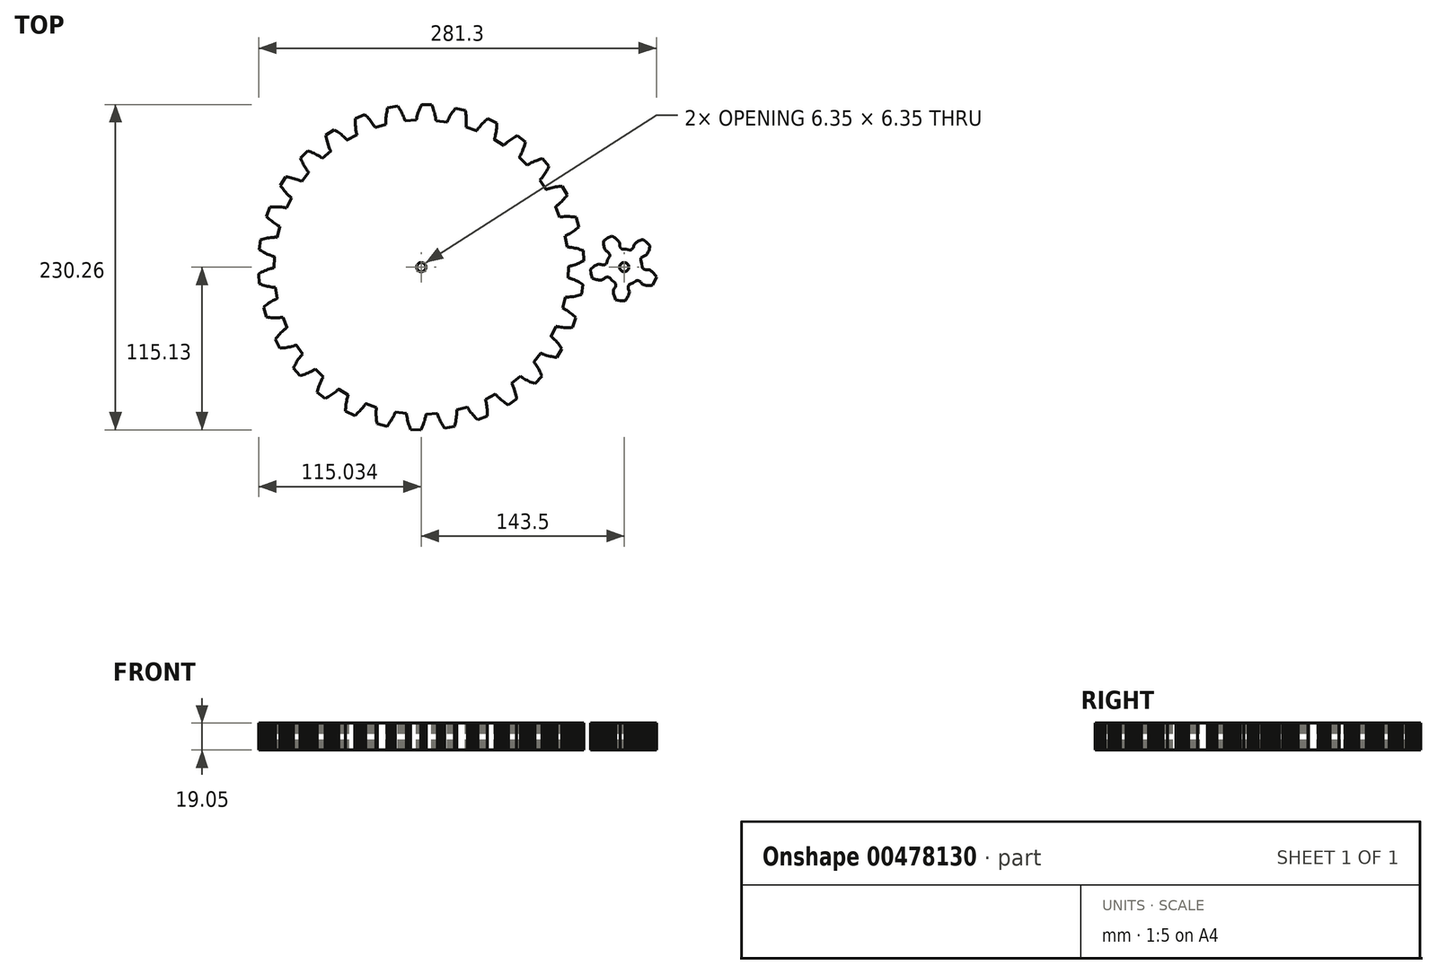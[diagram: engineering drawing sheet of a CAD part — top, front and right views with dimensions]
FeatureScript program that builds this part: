
annotation { "Feature Type Name" : "Feature", "Feature Type Description" : "" }
export const myFeature = defineFeature(function(context is Context, id is Id, definition is map)
    precondition{}
    {
        {
            var Q0;
            Q0=qCreatedBy(makeId("Top.planeOp"),FACE);
            var sketch = newSketch(context, id + "F0", { "sketchPlane" : qUnion([Q0])});
            skLineSegment(sketch, "E0", {"start": v(78.23, -7.5) * mm, "end": v(78.5, -7.55) * mm});
            skLineSegment(sketch, "E1", {"start": v(78.5, -7.55) * mm, "end": v(78.77, -7.62) * mm});
            skLineSegment(sketch, "E2", {"start": v(78.77, -7.62) * mm, "end": v(79.04, -7.7) * mm});
            skLineSegment(sketch, "E3", {"start": v(79.04, -7.7) * mm, "end": v(79.31, -7.77) * mm});
            skLineSegment(sketch, "E4", {"start": v(79.31, -7.77) * mm, "end": v(79.85, -7.93) * mm});
            skLineSegment(sketch, "E5", {"start": v(79.85, -7.93) * mm, "end": v(80.4, -8.1) * mm});
            skLineSegment(sketch, "E6", {"start": v(80.4, -8.1) * mm, "end": v(81.47, -8.5) * mm});
            skLineSegment(sketch, "E7", {"start": v(81.47, -8.5) * mm, "end": v(82.54, -8.93) * mm});
            skLineSegment(sketch, "E8", {"start": v(82.54, -8.93) * mm, "end": v(83.6, -9.4) * mm});
            skLineSegment(sketch, "E9", {"start": v(83.6, -9.4) * mm, "end": v(84.66, -9.91) * mm});
            skLineSegment(sketch, "E10", {"start": v(84.66, -9.91) * mm, "end": v(85.72, -10.46) * mm});
            skLineSegment(sketch, "E11", {"start": v(85.72, -10.46) * mm, "end": v(86.77, -11.05) * mm});
            skLineSegment(sketch, "E12", {"start": v(86.77, -11.05) * mm, "end": v(87.81, -11.66) * mm});
            skLineSegment(sketch, "E13", {"start": v(87.81, -11.66) * mm, "end": v(88.85, -12.31) * mm});
            skLineSegment(sketch, "E14", {"start": v(88.85, -12.31) * mm, "end": v(87.87, -19.4) * mm});
            skLineSegment(sketch, "E15", {"start": v(87.87, -19.4) * mm, "end": v(86.7, -19.74) * mm});
            skLineSegment(sketch, "E16", {"start": v(86.7, -19.74) * mm, "end": v(85.52, -20.05) * mm});
            skLineSegment(sketch, "E17", {"start": v(85.52, -20.05) * mm, "end": v(84.35, -20.32) * mm});
            skLineSegment(sketch, "E18", {"start": v(84.35, -20.32) * mm, "end": v(83.18, -20.56) * mm});
            skLineSegment(sketch, "E19", {"start": v(83.18, -20.56) * mm, "end": v(82.02, -20.77) * mm});
            skLineSegment(sketch, "E20", {"start": v(82.02, -20.77) * mm, "end": v(80.87, -20.93) * mm});
            skLineSegment(sketch, "E21", {"start": v(80.87, -20.93) * mm, "end": v(79.72, -21.06) * mm});
            skLineSegment(sketch, "E22", {"start": v(79.72, -21.06) * mm, "end": v(78.58, -21.14) * mm});
            skLineSegment(sketch, "E23", {"start": v(78.58, -21.14) * mm, "end": v(78.01, -21.16) * mm});
            skLineSegment(sketch, "E24", {"start": v(78.01, -21.16) * mm, "end": v(77.45, -21.17) * mm});
            skLineSegment(sketch, "E25", {"start": v(77.45, -21.17) * mm, "end": v(77.17, -21.17) * mm});
            skLineSegment(sketch, "E26", {"start": v(77.17, -21.17) * mm, "end": v(76.89, -21.16) * mm});
            skLineSegment(sketch, "E27", {"start": v(76.89, -21.16) * mm, "end": v(76.6, -21.15) * mm});
            skLineSegment(sketch, "E28", {"start": v(76.6, -21.15) * mm, "end": v(76.33, -21.14) * mm});
            skLineSegment(sketch, "E29", {"start": v(76.33, -21.14) * mm, "end": v(74.4, -28.92) * mm});
            skLineSegment(sketch, "E30", {"start": v(74.4, -28.92) * mm, "end": v(74.65, -29.03) * mm});
            skLineSegment(sketch, "E31", {"start": v(74.65, -29.03) * mm, "end": v(74.9, -29.16) * mm});
            skLineSegment(sketch, "E32", {"start": v(74.9, -29.16) * mm, "end": v(75.16, -29.28) * mm});
            skLineSegment(sketch, "E33", {"start": v(75.16, -29.28) * mm, "end": v(75.4, -29.41) * mm});
            skLineSegment(sketch, "E34", {"start": v(75.4, -29.41) * mm, "end": v(75.9, -29.68) * mm});
            skLineSegment(sketch, "E35", {"start": v(75.9, -29.68) * mm, "end": v(76.39, -29.97) * mm});
            skLineSegment(sketch, "E36", {"start": v(76.39, -29.97) * mm, "end": v(77.36, -30.57) * mm});
            skLineSegment(sketch, "E37", {"start": v(77.36, -30.57) * mm, "end": v(78.32, -31.22) * mm});
            skLineSegment(sketch, "E38", {"start": v(78.32, -31.22) * mm, "end": v(79.26, -31.9) * mm});
            skLineSegment(sketch, "E39", {"start": v(79.26, -31.9) * mm, "end": v(80.2, -32.63) * mm});
            skLineSegment(sketch, "E40", {"start": v(80.2, -32.63) * mm, "end": v(81.11, -33.38) * mm});
            skLineSegment(sketch, "E41", {"start": v(81.11, -33.38) * mm, "end": v(82.02, -34.17) * mm});
            skLineSegment(sketch, "E42", {"start": v(82.02, -34.17) * mm, "end": v(82.91, -35) * mm});
            skLineSegment(sketch, "E43", {"start": v(82.91, -35) * mm, "end": v(83.8, -35.84) * mm});
            skLineSegment(sketch, "E44", {"start": v(83.8, -35.84) * mm, "end": v(81.35, -42.57) * mm});
            skLineSegment(sketch, "E45", {"start": v(81.35, -42.57) * mm, "end": v(80.13, -42.66) * mm});
            skLineSegment(sketch, "E46", {"start": v(80.13, -42.66) * mm, "end": v(78.92, -42.72) * mm});
            skLineSegment(sketch, "E47", {"start": v(78.92, -42.72) * mm, "end": v(77.72, -42.74) * mm});
            skLineSegment(sketch, "E48", {"start": v(77.72, -42.74) * mm, "end": v(76.53, -42.73) * mm});
            skLineSegment(sketch, "E49", {"start": v(76.53, -42.73) * mm, "end": v(75.35, -42.7) * mm});
            skLineSegment(sketch, "E50", {"start": v(75.35, -42.7) * mm, "end": v(74.19, -42.61) * mm});
            skLineSegment(sketch, "E51", {"start": v(74.19, -42.61) * mm, "end": v(73.04, -42.5) * mm});
            skLineSegment(sketch, "E52", {"start": v(73.04, -42.5) * mm, "end": v(71.9, -42.34) * mm});
            skLineSegment(sketch, "E53", {"start": v(71.9, -42.34) * mm, "end": v(71.35, -42.24) * mm});
            skLineSegment(sketch, "E54", {"start": v(71.35, -42.24) * mm, "end": v(70.8, -42.13) * mm});
            skLineSegment(sketch, "E55", {"start": v(70.8, -42.13) * mm, "end": v(70.52, -42.07) * mm});
            skLineSegment(sketch, "E56", {"start": v(70.52, -42.07) * mm, "end": v(70.25, -42.01) * mm});
            skLineSegment(sketch, "E57", {"start": v(70.25, -42.01) * mm, "end": v(69.98, -41.94) * mm});
            skLineSegment(sketch, "E58", {"start": v(69.98, -41.94) * mm, "end": v(69.7, -41.87) * mm});
            skLineSegment(sketch, "E59", {"start": v(69.7, -41.87) * mm, "end": v(66.2, -49.08) * mm});
            skLineSegment(sketch, "E60", {"start": v(66.2, -49.08) * mm, "end": v(66.43, -49.25) * mm});
            skLineSegment(sketch, "E61", {"start": v(66.43, -49.25) * mm, "end": v(66.65, -49.42) * mm});
            skLineSegment(sketch, "E62", {"start": v(66.65, -49.42) * mm, "end": v(66.87, -49.6) * mm});
            skLineSegment(sketch, "E63", {"start": v(66.87, -49.6) * mm, "end": v(67.08, -49.77) * mm});
            skLineSegment(sketch, "E64", {"start": v(67.08, -49.77) * mm, "end": v(67.5, -50.14) * mm});
            skLineSegment(sketch, "E65", {"start": v(67.5, -50.14) * mm, "end": v(67.93, -50.52) * mm});
            skLineSegment(sketch, "E66", {"start": v(67.93, -50.52) * mm, "end": v(68.75, -51.31) * mm});
            skLineSegment(sketch, "E67", {"start": v(68.75, -51.31) * mm, "end": v(69.56, -52.15) * mm});
            skLineSegment(sketch, "E68", {"start": v(69.56, -52.15) * mm, "end": v(70.34, -53.01) * mm});
            skLineSegment(sketch, "E69", {"start": v(70.34, -53.01) * mm, "end": v(71.1, -53.91) * mm});
            skLineSegment(sketch, "E70", {"start": v(71.1, -53.91) * mm, "end": v(71.84, -54.84) * mm});
            skLineSegment(sketch, "E71", {"start": v(71.84, -54.84) * mm, "end": v(72.56, -55.8) * mm});
            skLineSegment(sketch, "E72", {"start": v(72.56, -55.8) * mm, "end": v(73.26, -56.8) * mm});
            skLineSegment(sketch, "E73", {"start": v(73.26, -56.8) * mm, "end": v(73.95, -57.8) * mm});
            skLineSegment(sketch, "E74", {"start": v(73.95, -57.8) * mm, "end": v(70.17, -63.88) * mm});
            skLineSegment(sketch, "E75", {"start": v(70.17, -63.88) * mm, "end": v(68.95, -63.71) * mm});
            skLineSegment(sketch, "E76", {"start": v(68.95, -63.71) * mm, "end": v(67.75, -63.52) * mm});
            skLineSegment(sketch, "E77", {"start": v(67.75, -63.52) * mm, "end": v(66.57, -63.3) * mm});
            skLineSegment(sketch, "E78", {"start": v(66.57, -63.3) * mm, "end": v(65.41, -63.04) * mm});
            skLineSegment(sketch, "E79", {"start": v(65.41, -63.04) * mm, "end": v(64.27, -62.75) * mm});
            skLineSegment(sketch, "E80", {"start": v(64.27, -62.75) * mm, "end": v(63.15, -62.43) * mm});
            skLineSegment(sketch, "E81", {"start": v(63.15, -62.43) * mm, "end": v(62.05, -62.08) * mm});
            skLineSegment(sketch, "E82", {"start": v(62.05, -62.08) * mm, "end": v(60.97, -61.69) * mm});
            skLineSegment(sketch, "E83", {"start": v(60.97, -61.69) * mm, "end": v(60.45, -61.48) * mm});
            skLineSegment(sketch, "E84", {"start": v(60.45, -61.48) * mm, "end": v(59.93, -61.26) * mm});
            skLineSegment(sketch, "E85", {"start": v(59.93, -61.26) * mm, "end": v(59.67, -61.14) * mm});
            skLineSegment(sketch, "E86", {"start": v(59.67, -61.14) * mm, "end": v(59.42, -61.02) * mm});
            skLineSegment(sketch, "E87", {"start": v(59.42, -61.02) * mm, "end": v(59.17, -60.9) * mm});
            skLineSegment(sketch, "E88", {"start": v(59.17, -60.9) * mm, "end": v(58.92, -60.78) * mm});
            skLineSegment(sketch, "E89", {"start": v(58.92, -60.78) * mm, "end": v(54, -67.1) * mm});
            skLineSegment(sketch, "E90", {"start": v(54, -67.1) * mm, "end": v(54.18, -67.3) * mm});
            skLineSegment(sketch, "E91", {"start": v(54.18, -67.3) * mm, "end": v(54.36, -67.52) * mm});
            skLineSegment(sketch, "E92", {"start": v(54.36, -67.52) * mm, "end": v(54.53, -67.74) * mm});
            skLineSegment(sketch, "E93", {"start": v(54.53, -67.74) * mm, "end": v(54.7, -67.96) * mm});
            skLineSegment(sketch, "E94", {"start": v(54.7, -67.96) * mm, "end": v(55.05, -68.4) * mm});
            skLineSegment(sketch, "E95", {"start": v(55.05, -68.4) * mm, "end": v(55.38, -68.87) * mm});
            skLineSegment(sketch, "E96", {"start": v(55.38, -68.87) * mm, "end": v(56.02, -69.81) * mm});
            skLineSegment(sketch, "E97", {"start": v(56.02, -69.81) * mm, "end": v(56.63, -70.8) * mm});
            skLineSegment(sketch, "E98", {"start": v(56.63, -70.8) * mm, "end": v(57.22, -71.8) * mm});
            skLineSegment(sketch, "E99", {"start": v(57.22, -71.8) * mm, "end": v(57.77, -72.84) * mm});
            skLineSegment(sketch, "E100", {"start": v(57.77, -72.84) * mm, "end": v(58.3, -73.9) * mm});
            skLineSegment(sketch, "E101", {"start": v(58.3, -73.9) * mm, "end": v(58.81, -75) * mm});
            skLineSegment(sketch, "E102", {"start": v(58.81, -75) * mm, "end": v(59.3, -76.1) * mm});
            skLineSegment(sketch, "E103", {"start": v(59.3, -76.1) * mm, "end": v(59.76, -77.24) * mm});
            skLineSegment(sketch, "E104", {"start": v(59.76, -77.24) * mm, "end": v(54.8, -82.4) * mm});
            skLineSegment(sketch, "E105", {"start": v(54.8, -82.4) * mm, "end": v(53.64, -81.98) * mm});
            skLineSegment(sketch, "E106", {"start": v(53.64, -81.98) * mm, "end": v(52.5, -81.54) * mm});
            skLineSegment(sketch, "E107", {"start": v(52.5, -81.54) * mm, "end": v(51.4, -81.08) * mm});
            skLineSegment(sketch, "E108", {"start": v(51.4, -81.08) * mm, "end": v(50.32, -80.59) * mm});
            skLineSegment(sketch, "E109", {"start": v(50.32, -80.59) * mm, "end": v(49.26, -80.07) * mm});
            skLineSegment(sketch, "E110", {"start": v(49.26, -80.07) * mm, "end": v(48.23, -79.52) * mm});
            skLineSegment(sketch, "E111", {"start": v(48.23, -79.52) * mm, "end": v(47.22, -78.95) * mm});
            skLineSegment(sketch, "E112", {"start": v(47.22, -78.95) * mm, "end": v(46.25, -78.34) * mm});
            skLineSegment(sketch, "E113", {"start": v(46.25, -78.34) * mm, "end": v(45.78, -78.03) * mm});
            skLineSegment(sketch, "E114", {"start": v(45.78, -78.03) * mm, "end": v(45.32, -77.7) * mm});
            skLineSegment(sketch, "E115", {"start": v(45.32, -77.7) * mm, "end": v(45.1, -77.54) * mm});
            skLineSegment(sketch, "E116", {"start": v(45.1, -77.54) * mm, "end": v(44.87, -77.37) * mm});
            skLineSegment(sketch, "E117", {"start": v(44.87, -77.37) * mm, "end": v(44.65, -77.2) * mm});
            skLineSegment(sketch, "E118", {"start": v(44.65, -77.2) * mm, "end": v(44.43, -77.02) * mm});
            skLineSegment(sketch, "E119", {"start": v(44.43, -77.02) * mm, "end": v(38.3, -82.18) * mm});
            skLineSegment(sketch, "E120", {"start": v(38.3, -82.18) * mm, "end": v(38.44, -82.43) * mm});
            skLineSegment(sketch, "E121", {"start": v(38.44, -82.43) * mm, "end": v(38.57, -82.67) * mm});
            skLineSegment(sketch, "E122", {"start": v(38.57, -82.67) * mm, "end": v(38.7, -82.92) * mm});
            skLineSegment(sketch, "E123", {"start": v(38.7, -82.92) * mm, "end": v(38.82, -83.17) * mm});
            skLineSegment(sketch, "E124", {"start": v(38.82, -83.17) * mm, "end": v(39.06, -83.68) * mm});
            skLineSegment(sketch, "E125", {"start": v(39.06, -83.68) * mm, "end": v(39.3, -84.2) * mm});
            skLineSegment(sketch, "E126", {"start": v(39.3, -84.2) * mm, "end": v(39.72, -85.26) * mm});
            skLineSegment(sketch, "E127", {"start": v(39.72, -85.26) * mm, "end": v(40.12, -86.35) * mm});
            skLineSegment(sketch, "E128", {"start": v(40.12, -86.35) * mm, "end": v(40.48, -87.46) * mm});
            skLineSegment(sketch, "E129", {"start": v(40.48, -87.46) * mm, "end": v(40.8, -88.59) * mm});
            skLineSegment(sketch, "E130", {"start": v(40.8, -88.59) * mm, "end": v(41.1, -89.74) * mm});
            skLineSegment(sketch, "E131", {"start": v(41.1, -89.74) * mm, "end": v(41.37, -90.91) * mm});
            skLineSegment(sketch, "E132", {"start": v(41.37, -90.91) * mm, "end": v(41.62, -92.1) * mm});
            skLineSegment(sketch, "E133", {"start": v(41.62, -92.1) * mm, "end": v(41.83, -93.3) * mm});
            skLineSegment(sketch, "E134", {"start": v(41.83, -93.3) * mm, "end": v(35.9, -97.32) * mm});
            skLineSegment(sketch, "E135", {"start": v(35.9, -97.32) * mm, "end": v(34.86, -96.67) * mm});
            skLineSegment(sketch, "E136", {"start": v(34.86, -96.67) * mm, "end": v(33.85, -96) * mm});
            skLineSegment(sketch, "E137", {"start": v(33.85, -96) * mm, "end": v(32.86, -95.32) * mm});
            skLineSegment(sketch, "E138", {"start": v(32.86, -95.32) * mm, "end": v(31.9, -94.61) * mm});
            skLineSegment(sketch, "E139", {"start": v(31.9, -94.61) * mm, "end": v(30.97, -93.89) * mm});
            skLineSegment(sketch, "E140", {"start": v(30.97, -93.89) * mm, "end": v(30.08, -93.14) * mm});
            skLineSegment(sketch, "E141", {"start": v(30.08, -93.14) * mm, "end": v(29.22, -92.37) * mm});
            skLineSegment(sketch, "E142", {"start": v(29.22, -92.37) * mm, "end": v(28.4, -91.58) * mm});
            skLineSegment(sketch, "E143", {"start": v(28.4, -91.58) * mm, "end": v(28, -91.17) * mm});
            skLineSegment(sketch, "E144", {"start": v(28, -91.17) * mm, "end": v(27.62, -90.76) * mm});
            skLineSegment(sketch, "E145", {"start": v(27.62, -90.76) * mm, "end": v(27.43, -90.55) * mm});
            skLineSegment(sketch, "E146", {"start": v(27.43, -90.55) * mm, "end": v(27.25, -90.33) * mm});
            skLineSegment(sketch, "E147", {"start": v(27.25, -90.33) * mm, "end": v(27.07, -90.12) * mm});
            skLineSegment(sketch, "E148", {"start": v(27.07, -90.12) * mm, "end": v(26.89, -89.9) * mm});
            skLineSegment(sketch, "E149", {"start": v(26.89, -89.9) * mm, "end": v(19.82, -93.68) * mm});
            skLineSegment(sketch, "E150", {"start": v(19.82, -93.68) * mm, "end": v(19.9, -93.94) * mm});
            skLineSegment(sketch, "E151", {"start": v(19.9, -93.94) * mm, "end": v(19.98, -94.21) * mm});
            skLineSegment(sketch, "E152", {"start": v(19.98, -94.21) * mm, "end": v(20.05, -94.48) * mm});
            skLineSegment(sketch, "E153", {"start": v(20.05, -94.48) * mm, "end": v(20.12, -94.75) * mm});
            skLineSegment(sketch, "E154", {"start": v(20.12, -94.75) * mm, "end": v(20.25, -95.3) * mm});
            skLineSegment(sketch, "E155", {"start": v(20.25, -95.3) * mm, "end": v(20.37, -95.86) * mm});
            skLineSegment(sketch, "E156", {"start": v(20.37, -95.86) * mm, "end": v(20.57, -96.98) * mm});
            skLineSegment(sketch, "E157", {"start": v(20.57, -96.98) * mm, "end": v(20.73, -98.13) * mm});
            skLineSegment(sketch, "E158", {"start": v(20.73, -98.13) * mm, "end": v(20.85, -99.29) * mm});
            skLineSegment(sketch, "E159", {"start": v(20.85, -99.29) * mm, "end": v(20.94, -100.46) * mm});
            skLineSegment(sketch, "E160", {"start": v(20.94, -100.46) * mm, "end": v(20.99, -101.65) * mm});
            skLineSegment(sketch, "E161", {"start": v(20.99, -101.65) * mm, "end": v(21, -102.85) * mm});
            skLineSegment(sketch, "E162", {"start": v(21, -102.85) * mm, "end": v(21, -104.06) * mm});
            skLineSegment(sketch, "E163", {"start": v(21, -104.06) * mm, "end": v(20.96, -105.29) * mm});
            skLineSegment(sketch, "E164", {"start": v(20.96, -105.29) * mm, "end": v(14.32, -107.98) * mm});
            skLineSegment(sketch, "E165", {"start": v(14.32, -107.98) * mm, "end": v(13.44, -107.13) * mm});
            skLineSegment(sketch, "E166", {"start": v(13.44, -107.13) * mm, "end": v(12.59, -106.27) * mm});
            skLineSegment(sketch, "E167", {"start": v(12.59, -106.27) * mm, "end": v(11.77, -105.4) * mm});
            skLineSegment(sketch, "E168", {"start": v(11.77, -105.4) * mm, "end": v(10.97, -104.5) * mm});
            skLineSegment(sketch, "E169", {"start": v(10.97, -104.5) * mm, "end": v(10.22, -103.6) * mm});
            skLineSegment(sketch, "E170", {"start": v(10.22, -103.6) * mm, "end": v(9.5, -102.68) * mm});
            skLineSegment(sketch, "E171", {"start": v(9.5, -102.68) * mm, "end": v(8.82, -101.75) * mm});
            skLineSegment(sketch, "E172", {"start": v(8.82, -101.75) * mm, "end": v(8.18, -100.8) * mm});
            skLineSegment(sketch, "E173", {"start": v(8.18, -100.8) * mm, "end": v(7.87, -100.32) * mm});
            skLineSegment(sketch, "E174", {"start": v(7.87, -100.32) * mm, "end": v(7.58, -99.84) * mm});
            skLineSegment(sketch, "E175", {"start": v(7.58, -99.84) * mm, "end": v(7.44, -99.6) * mm});
            skLineSegment(sketch, "E176", {"start": v(7.44, -99.6) * mm, "end": v(7.3, -99.35) * mm});
            skLineSegment(sketch, "E177", {"start": v(7.3, -99.35) * mm, "end": v(7.18, -99.1) * mm});
            skLineSegment(sketch, "E178", {"start": v(7.18, -99.1) * mm, "end": v(7.05, -98.86) * mm});
            skLineSegment(sketch, "E179", {"start": v(7.05, -98.86) * mm, "end": v(-0.65, -101.08) * mm});
            skLineSegment(sketch, "E180", {"start": v(-0.65, -101.08) * mm, "end": v(-0.63, -101.35) * mm});
            skLineSegment(sketch, "E181", {"start": v(-0.63, -101.35) * mm, "end": v(-0.6, -101.63) * mm});
            skLineSegment(sketch, "E182", {"start": v(-0.6, -101.63) * mm, "end": v(-0.6, -101.91) * mm});
            skLineSegment(sketch, "E183", {"start": v(-0.6, -101.91) * mm, "end": v(-0.58, -102.2) * mm});
            skLineSegment(sketch, "E184", {"start": v(-0.58, -102.2) * mm, "end": v(-0.57, -102.76) * mm});
            skLineSegment(sketch, "E185", {"start": v(-0.57, -102.76) * mm, "end": v(-0.57, -103.32) * mm});
            skLineSegment(sketch, "E186", {"start": v(-0.57, -103.32) * mm, "end": v(-0.6, -104.47) * mm});
            skLineSegment(sketch, "E187", {"start": v(-0.6, -104.47) * mm, "end": v(-0.69, -105.62) * mm});
            skLineSegment(sketch, "E188", {"start": v(-0.69, -105.62) * mm, "end": v(-0.8, -106.78) * mm});
            skLineSegment(sketch, "E189", {"start": v(-0.8, -106.78) * mm, "end": v(-0.97, -107.94) * mm});
            skLineSegment(sketch, "E190", {"start": v(-0.97, -107.94) * mm, "end": v(-1.16, -109.12) * mm});
            skLineSegment(sketch, "E191", {"start": v(-1.16, -109.12) * mm, "end": v(-1.4, -110.3) * mm});
            skLineSegment(sketch, "E192", {"start": v(-1.4, -110.3) * mm, "end": v(-1.66, -111.48) * mm});
            skLineSegment(sketch, "E193", {"start": v(-1.66, -111.48) * mm, "end": v(-1.95, -112.67) * mm});
            skLineSegment(sketch, "E194", {"start": v(-1.95, -112.67) * mm, "end": v(-9, -113.92) * mm});
            skLineSegment(sketch, "E195", {"start": v(-9, -113.92) * mm, "end": v(-9.69, -112.9) * mm});
            skLineSegment(sketch, "E196", {"start": v(-9.69, -112.9) * mm, "end": v(-10.34, -111.89) * mm});
            skLineSegment(sketch, "E197", {"start": v(-10.34, -111.89) * mm, "end": v(-10.96, -110.86) * mm});
            skLineSegment(sketch, "E198", {"start": v(-10.96, -110.86) * mm, "end": v(-11.55, -109.83) * mm});
            skLineSegment(sketch, "E199", {"start": v(-11.55, -109.83) * mm, "end": v(-12.1, -108.79) * mm});
            skLineSegment(sketch, "E200", {"start": v(-12.1, -108.79) * mm, "end": v(-12.62, -107.74) * mm});
            skLineSegment(sketch, "E201", {"start": v(-12.62, -107.74) * mm, "end": v(-13.1, -106.69) * mm});
            skLineSegment(sketch, "E202", {"start": v(-13.1, -106.69) * mm, "end": v(-13.52, -105.63) * mm});
            skLineSegment(sketch, "E203", {"start": v(-13.52, -105.63) * mm, "end": v(-13.72, -105.1) * mm});
            skLineSegment(sketch, "E204", {"start": v(-13.72, -105.1) * mm, "end": v(-13.9, -104.56) * mm});
            skLineSegment(sketch, "E205", {"start": v(-13.9, -104.56) * mm, "end": v(-13.99, -104.3) * mm});
            skLineSegment(sketch, "E206", {"start": v(-13.99, -104.3) * mm, "end": v(-14.07, -104.03) * mm});
            skLineSegment(sketch, "E207", {"start": v(-14.07, -104.03) * mm, "end": v(-14.14, -103.76) * mm});
            skLineSegment(sketch, "E208", {"start": v(-14.14, -103.76) * mm, "end": v(-14.22, -103.49) * mm});
            skLineSegment(sketch, "E209", {"start": v(-14.22, -103.49) * mm, "end": v(-22.21, -104.06) * mm});
            skLineSegment(sketch, "E210", {"start": v(-22.21, -104.06) * mm, "end": v(-22.24, -104.33) * mm});
            skLineSegment(sketch, "E211", {"start": v(-22.24, -104.33) * mm, "end": v(-22.28, -104.61) * mm});
            skLineSegment(sketch, "E212", {"start": v(-22.28, -104.61) * mm, "end": v(-22.33, -104.89) * mm});
            skLineSegment(sketch, "E213", {"start": v(-22.33, -104.89) * mm, "end": v(-22.37, -105.17) * mm});
            skLineSegment(sketch, "E214", {"start": v(-22.37, -105.17) * mm, "end": v(-22.48, -105.72) * mm});
            skLineSegment(sketch, "E215", {"start": v(-22.48, -105.72) * mm, "end": v(-22.6, -106.27) * mm});
            skLineSegment(sketch, "E216", {"start": v(-22.6, -106.27) * mm, "end": v(-22.87, -107.38) * mm});
            skLineSegment(sketch, "E217", {"start": v(-22.87, -107.38) * mm, "end": v(-23.19, -108.5) * mm});
            skLineSegment(sketch, "E218", {"start": v(-23.19, -108.5) * mm, "end": v(-23.55, -109.6) * mm});
            skLineSegment(sketch, "E219", {"start": v(-23.55, -109.6) * mm, "end": v(-23.95, -110.71) * mm});
            skLineSegment(sketch, "E220", {"start": v(-23.95, -110.71) * mm, "end": v(-24.38, -111.82) * mm});
            skLineSegment(sketch, "E221", {"start": v(-24.38, -111.82) * mm, "end": v(-24.85, -112.92) * mm});
            skLineSegment(sketch, "E222", {"start": v(-24.85, -112.92) * mm, "end": v(-25.36, -114.03) * mm});
            skLineSegment(sketch, "E223", {"start": v(-25.36, -114.03) * mm, "end": v(-25.9, -115.13) * mm});
            skLineSegment(sketch, "E224", {"start": v(-25.9, -115.13) * mm, "end": v(-33.05, -114.89) * mm});
            skLineSegment(sketch, "E225", {"start": v(-33.05, -114.89) * mm, "end": v(-33.5, -113.75) * mm});
            skLineSegment(sketch, "E226", {"start": v(-33.5, -113.75) * mm, "end": v(-33.94, -112.62) * mm});
            skLineSegment(sketch, "E227", {"start": v(-33.94, -112.62) * mm, "end": v(-34.33, -111.48) * mm});
            skLineSegment(sketch, "E228", {"start": v(-34.33, -111.48) * mm, "end": v(-34.7, -110.35) * mm});
            skLineSegment(sketch, "E229", {"start": v(-34.7, -110.35) * mm, "end": v(-35.02, -109.22) * mm});
            skLineSegment(sketch, "E230", {"start": v(-35.02, -109.22) * mm, "end": v(-35.3, -108.09) * mm});
            skLineSegment(sketch, "E231", {"start": v(-35.3, -108.09) * mm, "end": v(-35.55, -106.96) * mm});
            skLineSegment(sketch, "E232", {"start": v(-35.55, -106.96) * mm, "end": v(-35.75, -105.83) * mm});
            skLineSegment(sketch, "E233", {"start": v(-35.75, -105.83) * mm, "end": v(-35.83, -105.27) * mm});
            skLineSegment(sketch, "E234", {"start": v(-35.83, -105.27) * mm, "end": v(-35.9, -104.71) * mm});
            skLineSegment(sketch, "E235", {"start": v(-35.9, -104.71) * mm, "end": v(-35.92, -104.43) * mm});
            skLineSegment(sketch, "E236", {"start": v(-35.92, -104.43) * mm, "end": v(-35.95, -104.15) * mm});
            skLineSegment(sketch, "E237", {"start": v(-35.95, -104.15) * mm, "end": v(-35.97, -103.87) * mm});
            skLineSegment(sketch, "E238", {"start": v(-35.97, -103.87) * mm, "end": v(-35.98, -103.6) * mm});
            skLineSegment(sketch, "E239", {"start": v(-35.98, -103.6) * mm, "end": v(-43.92, -102.5) * mm});
            skLineSegment(sketch, "E240", {"start": v(-43.92, -102.5) * mm, "end": v(-44.01, -102.76) * mm});
            skLineSegment(sketch, "E241", {"start": v(-44.01, -102.76) * mm, "end": v(-44.1, -103.02) * mm});
            skLineSegment(sketch, "E242", {"start": v(-44.1, -103.02) * mm, "end": v(-44.2, -103.28) * mm});
            skLineSegment(sketch, "E243", {"start": v(-44.2, -103.28) * mm, "end": v(-44.3, -103.54) * mm});
            skLineSegment(sketch, "E244", {"start": v(-44.3, -103.54) * mm, "end": v(-44.53, -104.06) * mm});
            skLineSegment(sketch, "E245", {"start": v(-44.53, -104.06) * mm, "end": v(-44.76, -104.58) * mm});
            skLineSegment(sketch, "E246", {"start": v(-44.76, -104.58) * mm, "end": v(-45.26, -105.6) * mm});
            skLineSegment(sketch, "E247", {"start": v(-45.26, -105.6) * mm, "end": v(-45.8, -106.63) * mm});
            skLineSegment(sketch, "E248", {"start": v(-45.8, -106.63) * mm, "end": v(-46.38, -107.64) * mm});
            skLineSegment(sketch, "E249", {"start": v(-46.38, -107.64) * mm, "end": v(-47, -108.64) * mm});
            skLineSegment(sketch, "E250", {"start": v(-47, -108.64) * mm, "end": v(-47.66, -109.63) * mm});
            skLineSegment(sketch, "E251", {"start": v(-47.66, -109.63) * mm, "end": v(-48.35, -110.61) * mm});
            skLineSegment(sketch, "E252", {"start": v(-48.35, -110.61) * mm, "end": v(-49.07, -111.59) * mm});
            skLineSegment(sketch, "E253", {"start": v(-49.07, -111.59) * mm, "end": v(-49.83, -112.56) * mm});
            skLineSegment(sketch, "E254", {"start": v(-49.83, -112.56) * mm, "end": v(-56.77, -110.83) * mm});
            skLineSegment(sketch, "E255", {"start": v(-56.77, -110.83) * mm, "end": v(-56.99, -109.63) * mm});
            skLineSegment(sketch, "E256", {"start": v(-56.99, -109.63) * mm, "end": v(-57.17, -108.43) * mm});
            skLineSegment(sketch, "E257", {"start": v(-57.17, -108.43) * mm, "end": v(-57.32, -107.24) * mm});
            skLineSegment(sketch, "E258", {"start": v(-57.32, -107.24) * mm, "end": v(-57.44, -106.05) * mm});
            skLineSegment(sketch, "E259", {"start": v(-57.44, -106.05) * mm, "end": v(-57.52, -104.88) * mm});
            skLineSegment(sketch, "E260", {"start": v(-57.52, -104.88) * mm, "end": v(-57.56, -103.71) * mm});
            skLineSegment(sketch, "E261", {"start": v(-57.56, -103.71) * mm, "end": v(-57.57, -102.56) * mm});
            skLineSegment(sketch, "E262", {"start": v(-57.57, -102.56) * mm, "end": v(-57.53, -101.41) * mm});
            skLineSegment(sketch, "E263", {"start": v(-57.53, -101.41) * mm, "end": v(-57.5, -100.85) * mm});
            skLineSegment(sketch, "E264", {"start": v(-57.5, -100.85) * mm, "end": v(-57.44, -100.29) * mm});
            skLineSegment(sketch, "E265", {"start": v(-57.44, -100.29) * mm, "end": v(-57.41, -100) * mm});
            skLineSegment(sketch, "E266", {"start": v(-57.41, -100) * mm, "end": v(-57.38, -99.73) * mm});
            skLineSegment(sketch, "E267", {"start": v(-57.38, -99.73) * mm, "end": v(-57.34, -99.45) * mm});
            skLineSegment(sketch, "E268", {"start": v(-57.34, -99.45) * mm, "end": v(-57.3, -99.18) * mm});
            skLineSegment(sketch, "E269", {"start": v(-57.3, -99.18) * mm, "end": v(-64.83, -96.45) * mm});
            skLineSegment(sketch, "E270", {"start": v(-64.83, -96.45) * mm, "end": v(-64.97, -96.69) * mm});
            skLineSegment(sketch, "E271", {"start": v(-64.97, -96.69) * mm, "end": v(-65.12, -96.92) * mm});
            skLineSegment(sketch, "E272", {"start": v(-65.12, -96.92) * mm, "end": v(-65.27, -97.16) * mm});
            skLineSegment(sketch, "E273", {"start": v(-65.27, -97.16) * mm, "end": v(-65.43, -97.4) * mm});
            skLineSegment(sketch, "E274", {"start": v(-65.43, -97.4) * mm, "end": v(-65.75, -97.86) * mm});
            skLineSegment(sketch, "E275", {"start": v(-65.75, -97.86) * mm, "end": v(-66.08, -98.31) * mm});
            skLineSegment(sketch, "E276", {"start": v(-66.08, -98.31) * mm, "end": v(-66.78, -99.22) * mm});
            skLineSegment(sketch, "E277", {"start": v(-66.78, -99.22) * mm, "end": v(-67.53, -100.1) * mm});
            skLineSegment(sketch, "E278", {"start": v(-67.53, -100.1) * mm, "end": v(-68.3, -100.97) * mm});
            skLineSegment(sketch, "E279", {"start": v(-68.3, -100.97) * mm, "end": v(-69.12, -101.82) * mm});
            skLineSegment(sketch, "E280", {"start": v(-69.12, -101.82) * mm, "end": v(-69.97, -102.65) * mm});
            skLineSegment(sketch, "E281", {"start": v(-69.97, -102.65) * mm, "end": v(-70.85, -103.47) * mm});
            skLineSegment(sketch, "E282", {"start": v(-70.85, -103.47) * mm, "end": v(-71.76, -104.27) * mm});
            skLineSegment(sketch, "E283", {"start": v(-71.76, -104.27) * mm, "end": v(-72.7, -105.06) * mm});
            skLineSegment(sketch, "E284", {"start": v(-72.7, -105.06) * mm, "end": v(-79.13, -101.93) * mm});
            skLineSegment(sketch, "E285", {"start": v(-79.13, -101.93) * mm, "end": v(-79.1, -100.7) * mm});
            skLineSegment(sketch, "E286", {"start": v(-79.1, -100.7) * mm, "end": v(-79.03, -99.5) * mm});
            skLineSegment(sketch, "E287", {"start": v(-79.03, -99.5) * mm, "end": v(-78.92, -98.3) * mm});
            skLineSegment(sketch, "E288", {"start": v(-78.92, -98.3) * mm, "end": v(-78.8, -97.12) * mm});
            skLineSegment(sketch, "E289", {"start": v(-78.8, -97.12) * mm, "end": v(-78.63, -95.95) * mm});
            skLineSegment(sketch, "E290", {"start": v(-78.63, -95.95) * mm, "end": v(-78.43, -94.8) * mm});
            skLineSegment(sketch, "E291", {"start": v(-78.43, -94.8) * mm, "end": v(-78.2, -93.67) * mm});
            skLineSegment(sketch, "E292", {"start": v(-78.2, -93.67) * mm, "end": v(-77.92, -92.56) * mm});
            skLineSegment(sketch, "E293", {"start": v(-77.92, -92.56) * mm, "end": v(-77.76, -92.02) * mm});
            skLineSegment(sketch, "E294", {"start": v(-77.76, -92.02) * mm, "end": v(-77.6, -91.48) * mm});
            skLineSegment(sketch, "E295", {"start": v(-77.6, -91.48) * mm, "end": v(-77.5, -91.21) * mm});
            skLineSegment(sketch, "E296", {"start": v(-77.5, -91.21) * mm, "end": v(-77.42, -90.95) * mm});
            skLineSegment(sketch, "E297", {"start": v(-77.42, -90.95) * mm, "end": v(-77.32, -90.68) * mm});
            skLineSegment(sketch, "E298", {"start": v(-77.32, -90.68) * mm, "end": v(-77.22, -90.42) * mm});
            skLineSegment(sketch, "E299", {"start": v(-77.22, -90.42) * mm, "end": v(-84.02, -86.19) * mm});
            skLineSegment(sketch, "E300", {"start": v(-84.02, -86.19) * mm, "end": v(-84.21, -86.4) * mm});
            skLineSegment(sketch, "E301", {"start": v(-84.21, -86.4) * mm, "end": v(-84.4, -86.6) * mm});
            skLineSegment(sketch, "E302", {"start": v(-84.4, -86.6) * mm, "end": v(-84.6, -86.8) * mm});
            skLineSegment(sketch, "E303", {"start": v(-84.6, -86.8) * mm, "end": v(-84.8, -86.99) * mm});
            skLineSegment(sketch, "E304", {"start": v(-84.8, -86.99) * mm, "end": v(-85.22, -87.37) * mm});
            skLineSegment(sketch, "E305", {"start": v(-85.22, -87.37) * mm, "end": v(-85.64, -87.75) * mm});
            skLineSegment(sketch, "E306", {"start": v(-85.64, -87.75) * mm, "end": v(-86.51, -88.49) * mm});
            skLineSegment(sketch, "E307", {"start": v(-86.51, -88.49) * mm, "end": v(-87.42, -89.2) * mm});
            skLineSegment(sketch, "E308", {"start": v(-87.42, -89.2) * mm, "end": v(-88.37, -89.88) * mm});
            skLineSegment(sketch, "E309", {"start": v(-88.37, -89.88) * mm, "end": v(-89.34, -90.55) * mm});
            skLineSegment(sketch, "E310", {"start": v(-89.34, -90.55) * mm, "end": v(-90.34, -91.19) * mm});
            skLineSegment(sketch, "E311", {"start": v(-90.34, -91.19) * mm, "end": v(-91.38, -91.8) * mm});
            skLineSegment(sketch, "E312", {"start": v(-91.38, -91.8) * mm, "end": v(-92.43, -92.4) * mm});
            skLineSegment(sketch, "E313", {"start": v(-92.43, -92.4) * mm, "end": v(-93.51, -92.98) * mm});
            skLineSegment(sketch, "E314", {"start": v(-93.51, -92.98) * mm, "end": v(-99.16, -88.58) * mm});
            skLineSegment(sketch, "E315", {"start": v(-99.16, -88.58) * mm, "end": v(-98.86, -87.39) * mm});
            skLineSegment(sketch, "E316", {"start": v(-98.86, -87.39) * mm, "end": v(-98.54, -86.22) * mm});
            skLineSegment(sketch, "E317", {"start": v(-98.54, -86.22) * mm, "end": v(-98.2, -85.07) * mm});
            skLineSegment(sketch, "E318", {"start": v(-98.2, -85.07) * mm, "end": v(-97.82, -83.94) * mm});
            skLineSegment(sketch, "E319", {"start": v(-97.82, -83.94) * mm, "end": v(-97.42, -82.83) * mm});
            skLineSegment(sketch, "E320", {"start": v(-97.42, -82.83) * mm, "end": v(-96.98, -81.75) * mm});
            skLineSegment(sketch, "E321", {"start": v(-96.98, -81.75) * mm, "end": v(-96.52, -80.7) * mm});
            skLineSegment(sketch, "E322", {"start": v(-96.52, -80.7) * mm, "end": v(-96.02, -79.67) * mm});
            skLineSegment(sketch, "E323", {"start": v(-96.02, -79.67) * mm, "end": v(-95.75, -79.16) * mm});
            skLineSegment(sketch, "E324", {"start": v(-95.75, -79.16) * mm, "end": v(-95.48, -78.67) * mm});
            skLineSegment(sketch, "E325", {"start": v(-95.48, -78.67) * mm, "end": v(-95.34, -78.43) * mm});
            skLineSegment(sketch, "E326", {"start": v(-95.34, -78.43) * mm, "end": v(-95.2, -78.19) * mm});
            skLineSegment(sketch, "E327", {"start": v(-95.2, -78.19) * mm, "end": v(-95.05, -77.95) * mm});
            skLineSegment(sketch, "E328", {"start": v(-95.05, -77.95) * mm, "end": v(-94.9, -77.72) * mm});
            skLineSegment(sketch, "E329", {"start": v(-94.9, -77.72) * mm, "end": v(-100.67, -72.16) * mm});
            skLineSegment(sketch, "E330", {"start": v(-100.67, -72.16) * mm, "end": v(-100.9, -72.32) * mm});
            skLineSegment(sketch, "E331", {"start": v(-100.9, -72.32) * mm, "end": v(-101.13, -72.48) * mm});
            skLineSegment(sketch, "E332", {"start": v(-101.13, -72.48) * mm, "end": v(-101.36, -72.63) * mm});
            skLineSegment(sketch, "E333", {"start": v(-101.36, -72.63) * mm, "end": v(-101.6, -72.78) * mm});
            skLineSegment(sketch, "E334", {"start": v(-101.6, -72.78) * mm, "end": v(-102.08, -73.07) * mm});
            skLineSegment(sketch, "E335", {"start": v(-102.08, -73.07) * mm, "end": v(-102.57, -73.36) * mm});
            skLineSegment(sketch, "E336", {"start": v(-102.57, -73.36) * mm, "end": v(-103.58, -73.9) * mm});
            skLineSegment(sketch, "E337", {"start": v(-103.58, -73.9) * mm, "end": v(-104.62, -74.4) * mm});
            skLineSegment(sketch, "E338", {"start": v(-104.62, -74.4) * mm, "end": v(-105.68, -74.87) * mm});
            skLineSegment(sketch, "E339", {"start": v(-105.68, -74.87) * mm, "end": v(-106.77, -75.32) * mm});
            skLineSegment(sketch, "E340", {"start": v(-106.77, -75.32) * mm, "end": v(-107.89, -75.74) * mm});
            skLineSegment(sketch, "E341", {"start": v(-107.89, -75.74) * mm, "end": v(-109.03, -76.13) * mm});
            skLineSegment(sketch, "E342", {"start": v(-109.03, -76.13) * mm, "end": v(-110.18, -76.5) * mm});
            skLineSegment(sketch, "E343", {"start": v(-110.18, -76.5) * mm, "end": v(-111.36, -76.83) * mm});
            skLineSegment(sketch, "E344", {"start": v(-111.36, -76.83) * mm, "end": v(-115.97, -71.35) * mm});
            skLineSegment(sketch, "E345", {"start": v(-115.97, -71.35) * mm, "end": v(-115.43, -70.25) * mm});
            skLineSegment(sketch, "E346", {"start": v(-115.43, -70.25) * mm, "end": v(-114.88, -69.17) * mm});
            skLineSegment(sketch, "E347", {"start": v(-114.88, -69.17) * mm, "end": v(-114.3, -68.12) * mm});
            skLineSegment(sketch, "E348", {"start": v(-114.3, -68.12) * mm, "end": v(-113.7, -67.1) * mm});
            skLineSegment(sketch, "E349", {"start": v(-113.7, -67.1) * mm, "end": v(-113.07, -66.1) * mm});
            skLineSegment(sketch, "E350", {"start": v(-113.07, -66.1) * mm, "end": v(-112.42, -65.13) * mm});
            skLineSegment(sketch, "E351", {"start": v(-112.42, -65.13) * mm, "end": v(-111.75, -64.19) * mm});
            skLineSegment(sketch, "E352", {"start": v(-111.75, -64.19) * mm, "end": v(-111.04, -63.29) * mm});
            skLineSegment(sketch, "E353", {"start": v(-111.04, -63.29) * mm, "end": v(-110.68, -62.85) * mm});
            skLineSegment(sketch, "E354", {"start": v(-110.68, -62.85) * mm, "end": v(-110.31, -62.43) * mm});
            skLineSegment(sketch, "E355", {"start": v(-110.31, -62.43) * mm, "end": v(-110.12, -62.22) * mm});
            skLineSegment(sketch, "E356", {"start": v(-110.12, -62.22) * mm, "end": v(-109.93, -62.01) * mm});
            skLineSegment(sketch, "E357", {"start": v(-109.93, -62.01) * mm, "end": v(-109.74, -61.81) * mm});
            skLineSegment(sketch, "E358", {"start": v(-109.74, -61.81) * mm, "end": v(-109.54, -61.62) * mm});
            skLineSegment(sketch, "E359", {"start": v(-109.54, -61.62) * mm, "end": v(-114.03, -54.98) * mm});
            skLineSegment(sketch, "E360", {"start": v(-114.03, -54.98) * mm, "end": v(-114.29, -55.09) * mm});
            skLineSegment(sketch, "E361", {"start": v(-114.29, -55.09) * mm, "end": v(-114.55, -55.2) * mm});
            skLineSegment(sketch, "E362", {"start": v(-114.55, -55.2) * mm, "end": v(-114.8, -55.3) * mm});
            skLineSegment(sketch, "E363", {"start": v(-114.8, -55.3) * mm, "end": v(-115.07, -55.4) * mm});
            skLineSegment(sketch, "E364", {"start": v(-115.07, -55.4) * mm, "end": v(-115.6, -55.58) * mm});
            skLineSegment(sketch, "E365", {"start": v(-115.6, -55.58) * mm, "end": v(-116.14, -55.75) * mm});
            skLineSegment(sketch, "E366", {"start": v(-116.14, -55.75) * mm, "end": v(-117.24, -56.07) * mm});
            skLineSegment(sketch, "E367", {"start": v(-117.24, -56.07) * mm, "end": v(-118.36, -56.35) * mm});
            skLineSegment(sketch, "E368", {"start": v(-118.36, -56.35) * mm, "end": v(-119.5, -56.6) * mm});
            skLineSegment(sketch, "E369", {"start": v(-119.5, -56.6) * mm, "end": v(-120.66, -56.8) * mm});
            skLineSegment(sketch, "E370", {"start": v(-120.66, -56.8) * mm, "end": v(-121.84, -56.98) * mm});
            skLineSegment(sketch, "E371", {"start": v(-121.84, -56.98) * mm, "end": v(-123.03, -57.12) * mm});
            skLineSegment(sketch, "E372", {"start": v(-123.03, -57.12) * mm, "end": v(-124.24, -57.24) * mm});
            skLineSegment(sketch, "E373", {"start": v(-124.24, -57.24) * mm, "end": v(-125.46, -57.32) * mm});
            skLineSegment(sketch, "E374", {"start": v(-125.46, -57.32) * mm, "end": v(-128.83, -51) * mm});
            skLineSegment(sketch, "E375", {"start": v(-128.83, -51) * mm, "end": v(-128.08, -50.04) * mm});
            skLineSegment(sketch, "E376", {"start": v(-128.08, -50.04) * mm, "end": v(-127.3, -49.1) * mm});
            skLineSegment(sketch, "E377", {"start": v(-127.3, -49.1) * mm, "end": v(-126.52, -48.2) * mm});
            skLineSegment(sketch, "E378", {"start": v(-126.52, -48.2) * mm, "end": v(-125.72, -47.31) * mm});
            skLineSegment(sketch, "E379", {"start": v(-125.72, -47.31) * mm, "end": v(-124.9, -46.47) * mm});
            skLineSegment(sketch, "E380", {"start": v(-124.9, -46.47) * mm, "end": v(-124.07, -45.65) * mm});
            skLineSegment(sketch, "E381", {"start": v(-124.07, -45.65) * mm, "end": v(-123.21, -44.88) * mm});
            skLineSegment(sketch, "E382", {"start": v(-123.21, -44.88) * mm, "end": v(-122.34, -44.14) * mm});
            skLineSegment(sketch, "E383", {"start": v(-122.34, -44.14) * mm, "end": v(-121.9, -43.8) * mm});
            skLineSegment(sketch, "E384", {"start": v(-121.9, -43.8) * mm, "end": v(-121.44, -43.45) * mm});
            skLineSegment(sketch, "E385", {"start": v(-121.44, -43.45) * mm, "end": v(-121.21, -43.3) * mm});
            skLineSegment(sketch, "E386", {"start": v(-121.21, -43.3) * mm, "end": v(-120.98, -43.13) * mm});
            skLineSegment(sketch, "E387", {"start": v(-120.98, -43.13) * mm, "end": v(-120.75, -42.97) * mm});
            skLineSegment(sketch, "E388", {"start": v(-120.75, -42.97) * mm, "end": v(-120.52, -42.82) * mm});
            skLineSegment(sketch, "E389", {"start": v(-120.52, -42.82) * mm, "end": v(-123.53, -35.4) * mm});
            skLineSegment(sketch, "E390", {"start": v(-123.53, -35.4) * mm, "end": v(-123.8, -35.45) * mm});
            skLineSegment(sketch, "E391", {"start": v(-123.8, -35.45) * mm, "end": v(-124.08, -35.5) * mm});
            skLineSegment(sketch, "E392", {"start": v(-124.08, -35.5) * mm, "end": v(-124.35, -35.54) * mm});
            skLineSegment(sketch, "E393", {"start": v(-124.35, -35.54) * mm, "end": v(-124.63, -35.58) * mm});
            skLineSegment(sketch, "E394", {"start": v(-124.63, -35.58) * mm, "end": v(-125.2, -35.65) * mm});
            skLineSegment(sketch, "E395", {"start": v(-125.2, -35.65) * mm, "end": v(-125.76, -35.71) * mm});
            skLineSegment(sketch, "E396", {"start": v(-125.76, -35.71) * mm, "end": v(-126.9, -35.8) * mm});
            skLineSegment(sketch, "E397", {"start": v(-126.9, -35.8) * mm, "end": v(-128.05, -35.83) * mm});
            skLineSegment(sketch, "E398", {"start": v(-128.05, -35.83) * mm, "end": v(-129.22, -35.83) * mm});
            skLineSegment(sketch, "E399", {"start": v(-129.22, -35.83) * mm, "end": v(-130.4, -35.8) * mm});
            skLineSegment(sketch, "E400", {"start": v(-130.4, -35.8) * mm, "end": v(-131.58, -35.73) * mm});
            skLineSegment(sketch, "E401", {"start": v(-131.58, -35.73) * mm, "end": v(-132.78, -35.62) * mm});
            skLineSegment(sketch, "E402", {"start": v(-132.78, -35.62) * mm, "end": v(-133.98, -35.48) * mm});
            skLineSegment(sketch, "E403", {"start": v(-133.98, -35.48) * mm, "end": v(-135.2, -35.31) * mm});
            skLineSegment(sketch, "E404", {"start": v(-135.2, -35.31) * mm, "end": v(-137.18, -28.43) * mm});
            skLineSegment(sketch, "E405", {"start": v(-137.18, -28.43) * mm, "end": v(-136.24, -27.65) * mm});
            skLineSegment(sketch, "E406", {"start": v(-136.24, -27.65) * mm, "end": v(-135.3, -26.89) * mm});
            skLineSegment(sketch, "E407", {"start": v(-135.3, -26.89) * mm, "end": v(-134.34, -26.16) * mm});
            skLineSegment(sketch, "E408", {"start": v(-134.34, -26.16) * mm, "end": v(-133.37, -25.47) * mm});
            skLineSegment(sketch, "E409", {"start": v(-133.37, -25.47) * mm, "end": v(-132.4, -24.8) * mm});
            skLineSegment(sketch, "E410", {"start": v(-132.4, -24.8) * mm, "end": v(-131.4, -24.19) * mm});
            skLineSegment(sketch, "E411", {"start": v(-131.4, -24.19) * mm, "end": v(-130.4, -23.6) * mm});
            skLineSegment(sketch, "E412", {"start": v(-130.4, -23.6) * mm, "end": v(-129.4, -23.07) * mm});
            skLineSegment(sketch, "E413", {"start": v(-129.4, -23.07) * mm, "end": v(-128.9, -22.82) * mm});
            skLineSegment(sketch, "E414", {"start": v(-128.9, -22.82) * mm, "end": v(-128.38, -22.58) * mm});
            skLineSegment(sketch, "E415", {"start": v(-128.38, -22.58) * mm, "end": v(-128.12, -22.47) * mm});
            skLineSegment(sketch, "E416", {"start": v(-128.12, -22.47) * mm, "end": v(-127.86, -22.36) * mm});
            skLineSegment(sketch, "E417", {"start": v(-127.86, -22.36) * mm, "end": v(-127.6, -22.25) * mm});
            skLineSegment(sketch, "E418", {"start": v(-127.6, -22.25) * mm, "end": v(-127.35, -22.15) * mm});
            skLineSegment(sketch, "E419", {"start": v(-127.35, -22.15) * mm, "end": v(-128.75, -14.26) * mm});
            skLineSegment(sketch, "E420", {"start": v(-128.75, -14.26) * mm, "end": v(-129.03, -14.26) * mm});
            skLineSegment(sketch, "E421", {"start": v(-129.03, -14.26) * mm, "end": v(-129.3, -14.25) * mm});
            skLineSegment(sketch, "E422", {"start": v(-129.3, -14.25) * mm, "end": v(-129.59, -14.24) * mm});
            skLineSegment(sketch, "E423", {"start": v(-129.59, -14.24) * mm, "end": v(-129.87, -14.22) * mm});
            skLineSegment(sketch, "E424", {"start": v(-129.87, -14.22) * mm, "end": v(-130.43, -14.17) * mm});
            skLineSegment(sketch, "E425", {"start": v(-130.43, -14.17) * mm, "end": v(-131, -14.11) * mm});
            skLineSegment(sketch, "E426", {"start": v(-131, -14.11) * mm, "end": v(-132.12, -13.96) * mm});
            skLineSegment(sketch, "E427", {"start": v(-132.12, -13.96) * mm, "end": v(-133.26, -13.75) * mm});
            skLineSegment(sketch, "E428", {"start": v(-133.26, -13.75) * mm, "end": v(-134.4, -13.51) * mm});
            skLineSegment(sketch, "E429", {"start": v(-134.4, -13.51) * mm, "end": v(-135.55, -13.23) * mm});
            skLineSegment(sketch, "E430", {"start": v(-135.55, -13.23) * mm, "end": v(-136.7, -12.91) * mm});
            skLineSegment(sketch, "E431", {"start": v(-136.7, -12.91) * mm, "end": v(-137.84, -12.56) * mm});
            skLineSegment(sketch, "E432", {"start": v(-137.84, -12.56) * mm, "end": v(-139, -12.18) * mm});
            skLineSegment(sketch, "E433", {"start": v(-139, -12.18) * mm, "end": v(-140.14, -11.76) * mm});
            skLineSegment(sketch, "E434", {"start": v(-140.14, -11.76) * mm, "end": v(-140.65, -4.62) * mm});
            skLineSegment(sketch, "E435", {"start": v(-140.65, -4.62) * mm, "end": v(-139.57, -4.04) * mm});
            skLineSegment(sketch, "E436", {"start": v(-139.57, -4.04) * mm, "end": v(-138.49, -3.5) * mm});
            skLineSegment(sketch, "E437", {"start": v(-138.49, -3.5) * mm, "end": v(-137.4, -2.98) * mm});
            skLineSegment(sketch, "E438", {"start": v(-137.4, -2.98) * mm, "end": v(-136.31, -2.5) * mm});
            skLineSegment(sketch, "E439", {"start": v(-136.31, -2.5) * mm, "end": v(-135.22, -2.07) * mm});
            skLineSegment(sketch, "E440", {"start": v(-135.22, -2.07) * mm, "end": v(-134.12, -1.66) * mm});
            skLineSegment(sketch, "E441", {"start": v(-134.12, -1.66) * mm, "end": v(-133.03, -1.3) * mm});
            skLineSegment(sketch, "E442", {"start": v(-133.03, -1.3) * mm, "end": v(-131.93, -0.99) * mm});
            skLineSegment(sketch, "E443", {"start": v(-131.93, -0.99) * mm, "end": v(-131.38, -0.85) * mm});
            skLineSegment(sketch, "E444", {"start": v(-131.38, -0.85) * mm, "end": v(-130.83, -0.72) * mm});
            skLineSegment(sketch, "E445", {"start": v(-130.83, -0.72) * mm, "end": v(-130.55, -0.67) * mm});
            skLineSegment(sketch, "E446", {"start": v(-130.55, -0.67) * mm, "end": v(-130.28, -0.61) * mm});
            skLineSegment(sketch, "E447", {"start": v(-130.28, -0.61) * mm, "end": v(-130, -0.56) * mm});
            skLineSegment(sketch, "E448", {"start": v(-130, -0.56) * mm, "end": v(-129.73, -0.52) * mm});
            skLineSegment(sketch, "E449", {"start": v(-129.73, -0.52) * mm, "end": v(-129.46, 7.5) * mm});
            skLineSegment(sketch, "E450", {"start": v(-129.46, 7.5) * mm, "end": v(-129.73, 7.55) * mm});
            skLineSegment(sketch, "E451", {"start": v(-129.73, 7.55) * mm, "end": v(-130, 7.62) * mm});
            skLineSegment(sketch, "E452", {"start": v(-130, 7.62) * mm, "end": v(-130.27, 7.7) * mm});
            skLineSegment(sketch, "E453", {"start": v(-130.27, 7.7) * mm, "end": v(-130.54, 7.77) * mm});
            skLineSegment(sketch, "E454", {"start": v(-130.54, 7.77) * mm, "end": v(-131.08, 7.93) * mm});
            skLineSegment(sketch, "E455", {"start": v(-131.08, 7.93) * mm, "end": v(-131.62, 8.1) * mm});
            skLineSegment(sketch, "E456", {"start": v(-131.62, 8.1) * mm, "end": v(-132.7, 8.5) * mm});
            skLineSegment(sketch, "E457", {"start": v(-132.7, 8.5) * mm, "end": v(-133.77, 8.93) * mm});
            skLineSegment(sketch, "E458", {"start": v(-133.77, 8.93) * mm, "end": v(-134.83, 9.4) * mm});
            skLineSegment(sketch, "E459", {"start": v(-134.83, 9.4) * mm, "end": v(-135.9, 9.91) * mm});
            skLineSegment(sketch, "E460", {"start": v(-135.9, 9.91) * mm, "end": v(-136.95, 10.46) * mm});
            skLineSegment(sketch, "E461", {"start": v(-136.95, 10.46) * mm, "end": v(-138, 11.05) * mm});
            skLineSegment(sketch, "E462", {"start": v(-138, 11.05) * mm, "end": v(-139.05, 11.66) * mm});
            skLineSegment(sketch, "E463", {"start": v(-139.05, 11.66) * mm, "end": v(-140.09, 12.31) * mm});
            skLineSegment(sketch, "E464", {"start": v(-140.09, 12.31) * mm, "end": v(-139.1, 19.4) * mm});
            skLineSegment(sketch, "E465", {"start": v(-139.1, 19.4) * mm, "end": v(-137.92, 19.74) * mm});
            skLineSegment(sketch, "E466", {"start": v(-137.92, 19.74) * mm, "end": v(-136.75, 20.05) * mm});
            skLineSegment(sketch, "E467", {"start": v(-136.75, 20.05) * mm, "end": v(-135.58, 20.32) * mm});
            skLineSegment(sketch, "E468", {"start": v(-135.58, 20.32) * mm, "end": v(-134.41, 20.56) * mm});
            skLineSegment(sketch, "E469", {"start": v(-134.41, 20.56) * mm, "end": v(-133.25, 20.77) * mm});
            skLineSegment(sketch, "E470", {"start": v(-133.25, 20.77) * mm, "end": v(-132.1, 20.93) * mm});
            skLineSegment(sketch, "E471", {"start": v(-132.1, 20.93) * mm, "end": v(-130.95, 21.06) * mm});
            skLineSegment(sketch, "E472", {"start": v(-130.95, 21.06) * mm, "end": v(-129.81, 21.14) * mm});
            skLineSegment(sketch, "E473", {"start": v(-129.81, 21.14) * mm, "end": v(-129.24, 21.16) * mm});
            skLineSegment(sketch, "E474", {"start": v(-129.24, 21.16) * mm, "end": v(-128.68, 21.17) * mm});
            skLineSegment(sketch, "E475", {"start": v(-128.68, 21.17) * mm, "end": v(-128.4, 21.17) * mm});
            skLineSegment(sketch, "E476", {"start": v(-128.4, 21.17) * mm, "end": v(-128.12, 21.16) * mm});
            skLineSegment(sketch, "E477", {"start": v(-128.12, 21.16) * mm, "end": v(-127.84, 21.15) * mm});
            skLineSegment(sketch, "E478", {"start": v(-127.84, 21.15) * mm, "end": v(-127.56, 21.14) * mm});
            skLineSegment(sketch, "E479", {"start": v(-127.56, 21.14) * mm, "end": v(-125.63, 28.92) * mm});
            skLineSegment(sketch, "E480", {"start": v(-125.63, 28.92) * mm, "end": v(-125.89, 29.03) * mm});
            skLineSegment(sketch, "E481", {"start": v(-125.89, 29.03) * mm, "end": v(-126.14, 29.16) * mm});
            skLineSegment(sketch, "E482", {"start": v(-126.14, 29.16) * mm, "end": v(-126.39, 29.28) * mm});
            skLineSegment(sketch, "E483", {"start": v(-126.39, 29.28) * mm, "end": v(-126.64, 29.41) * mm});
            skLineSegment(sketch, "E484", {"start": v(-126.64, 29.41) * mm, "end": v(-127.13, 29.68) * mm});
            skLineSegment(sketch, "E485", {"start": v(-127.13, 29.68) * mm, "end": v(-127.62, 29.97) * mm});
            skLineSegment(sketch, "E486", {"start": v(-127.62, 29.97) * mm, "end": v(-128.6, 30.57) * mm});
            skLineSegment(sketch, "E487", {"start": v(-128.6, 30.57) * mm, "end": v(-129.55, 31.22) * mm});
            skLineSegment(sketch, "E488", {"start": v(-129.55, 31.22) * mm, "end": v(-130.5, 31.9) * mm});
            skLineSegment(sketch, "E489", {"start": v(-130.5, 31.9) * mm, "end": v(-131.42, 32.63) * mm});
            skLineSegment(sketch, "E490", {"start": v(-131.42, 32.63) * mm, "end": v(-132.34, 33.38) * mm});
            skLineSegment(sketch, "E491", {"start": v(-132.34, 33.38) * mm, "end": v(-133.25, 34.17) * mm});
            skLineSegment(sketch, "E492", {"start": v(-133.25, 34.17) * mm, "end": v(-134.14, 35) * mm});
            skLineSegment(sketch, "E493", {"start": v(-134.14, 35) * mm, "end": v(-135.02, 35.84) * mm});
            skLineSegment(sketch, "E494", {"start": v(-135.02, 35.84) * mm, "end": v(-132.59, 42.57) * mm});
            skLineSegment(sketch, "E495", {"start": v(-132.59, 42.57) * mm, "end": v(-131.36, 42.66) * mm});
            skLineSegment(sketch, "E496", {"start": v(-131.36, 42.66) * mm, "end": v(-130.15, 42.72) * mm});
            skLineSegment(sketch, "E497", {"start": v(-130.15, 42.72) * mm, "end": v(-128.95, 42.74) * mm});
            skLineSegment(sketch, "E498", {"start": v(-128.95, 42.74) * mm, "end": v(-127.76, 42.73) * mm});
            skLineSegment(sketch, "E499", {"start": v(-127.76, 42.73) * mm, "end": v(-126.58, 42.7) * mm});
            skLineSegment(sketch, "E500", {"start": v(-126.58, 42.7) * mm, "end": v(-125.42, 42.61) * mm});
            skLineSegment(sketch, "E501", {"start": v(-125.42, 42.61) * mm, "end": v(-124.27, 42.5) * mm});
            skLineSegment(sketch, "E502", {"start": v(-124.27, 42.5) * mm, "end": v(-123.14, 42.34) * mm});
            skLineSegment(sketch, "E503", {"start": v(-123.14, 42.34) * mm, "end": v(-122.58, 42.24) * mm});
            skLineSegment(sketch, "E504", {"start": v(-122.58, 42.24) * mm, "end": v(-122.03, 42.13) * mm});
            skLineSegment(sketch, "E505", {"start": v(-122.03, 42.13) * mm, "end": v(-121.75, 42.07) * mm});
            skLineSegment(sketch, "E506", {"start": v(-121.75, 42.07) * mm, "end": v(-121.48, 42.01) * mm});
            skLineSegment(sketch, "E507", {"start": v(-121.48, 42.01) * mm, "end": v(-121.2, 41.94) * mm});
            skLineSegment(sketch, "E508", {"start": v(-121.2, 41.94) * mm, "end": v(-120.94, 41.87) * mm});
            skLineSegment(sketch, "E509", {"start": v(-120.94, 41.87) * mm, "end": v(-117.44, 49.08) * mm});
            skLineSegment(sketch, "E510", {"start": v(-117.44, 49.08) * mm, "end": v(-117.66, 49.25) * mm});
            skLineSegment(sketch, "E511", {"start": v(-117.66, 49.25) * mm, "end": v(-117.88, 49.42) * mm});
            skLineSegment(sketch, "E512", {"start": v(-117.88, 49.42) * mm, "end": v(-118.1, 49.6) * mm});
            skLineSegment(sketch, "E513", {"start": v(-118.1, 49.6) * mm, "end": v(-118.31, 49.77) * mm});
            skLineSegment(sketch, "E514", {"start": v(-118.31, 49.77) * mm, "end": v(-118.74, 50.14) * mm});
            skLineSegment(sketch, "E515", {"start": v(-118.74, 50.14) * mm, "end": v(-119.16, 50.52) * mm});
            skLineSegment(sketch, "E516", {"start": v(-119.16, 50.52) * mm, "end": v(-119.99, 51.31) * mm});
            skLineSegment(sketch, "E517", {"start": v(-119.99, 51.31) * mm, "end": v(-120.79, 52.15) * mm});
            skLineSegment(sketch, "E518", {"start": v(-120.79, 52.15) * mm, "end": v(-121.57, 53.01) * mm});
            skLineSegment(sketch, "E519", {"start": v(-121.57, 53.01) * mm, "end": v(-122.33, 53.91) * mm});
            skLineSegment(sketch, "E520", {"start": v(-122.33, 53.91) * mm, "end": v(-123.07, 54.84) * mm});
            skLineSegment(sketch, "E521", {"start": v(-123.07, 54.84) * mm, "end": v(-123.8, 55.8) * mm});
            skLineSegment(sketch, "E522", {"start": v(-123.8, 55.8) * mm, "end": v(-124.5, 56.8) * mm});
            skLineSegment(sketch, "E523", {"start": v(-124.5, 56.8) * mm, "end": v(-125.18, 57.8) * mm});
            skLineSegment(sketch, "E524", {"start": v(-125.18, 57.8) * mm, "end": v(-121.4, 63.88) * mm});
            skLineSegment(sketch, "E525", {"start": v(-121.4, 63.88) * mm, "end": v(-120.18, 63.71) * mm});
            skLineSegment(sketch, "E526", {"start": v(-120.18, 63.71) * mm, "end": v(-118.99, 63.52) * mm});
            skLineSegment(sketch, "E527", {"start": v(-118.99, 63.52) * mm, "end": v(-117.8, 63.3) * mm});
            skLineSegment(sketch, "E528", {"start": v(-117.8, 63.3) * mm, "end": v(-116.64, 63.04) * mm});
            skLineSegment(sketch, "E529", {"start": v(-116.64, 63.04) * mm, "end": v(-115.5, 62.75) * mm});
            skLineSegment(sketch, "E530", {"start": v(-115.5, 62.75) * mm, "end": v(-114.38, 62.43) * mm});
            skLineSegment(sketch, "E531", {"start": v(-114.38, 62.43) * mm, "end": v(-113.28, 62.08) * mm});
            skLineSegment(sketch, "E532", {"start": v(-113.28, 62.08) * mm, "end": v(-112.2, 61.69) * mm});
            skLineSegment(sketch, "E533", {"start": v(-112.2, 61.69) * mm, "end": v(-111.68, 61.48) * mm});
            skLineSegment(sketch, "E534", {"start": v(-111.68, 61.48) * mm, "end": v(-111.16, 61.26) * mm});
            skLineSegment(sketch, "E535", {"start": v(-111.16, 61.26) * mm, "end": v(-110.9, 61.14) * mm});
            skLineSegment(sketch, "E536", {"start": v(-110.9, 61.14) * mm, "end": v(-110.65, 61.02) * mm});
            skLineSegment(sketch, "E537", {"start": v(-110.65, 61.02) * mm, "end": v(-110.4, 60.9) * mm});
            skLineSegment(sketch, "E538", {"start": v(-110.4, 60.9) * mm, "end": v(-110.15, 60.78) * mm});
            skLineSegment(sketch, "E539", {"start": v(-110.15, 60.78) * mm, "end": v(-105.23, 67.1) * mm});
            skLineSegment(sketch, "E540", {"start": v(-105.23, 67.1) * mm, "end": v(-105.4, 67.3) * mm});
            skLineSegment(sketch, "E541", {"start": v(-105.4, 67.3) * mm, "end": v(-105.59, 67.52) * mm});
            skLineSegment(sketch, "E542", {"start": v(-105.59, 67.52) * mm, "end": v(-105.76, 67.74) * mm});
            skLineSegment(sketch, "E543", {"start": v(-105.76, 67.74) * mm, "end": v(-105.94, 67.96) * mm});
            skLineSegment(sketch, "E544", {"start": v(-105.94, 67.96) * mm, "end": v(-106.28, 68.4) * mm});
            skLineSegment(sketch, "E545", {"start": v(-106.28, 68.4) * mm, "end": v(-106.61, 68.87) * mm});
            skLineSegment(sketch, "E546", {"start": v(-106.61, 68.87) * mm, "end": v(-107.25, 69.81) * mm});
            skLineSegment(sketch, "E547", {"start": v(-107.25, 69.81) * mm, "end": v(-107.87, 70.8) * mm});
            skLineSegment(sketch, "E548", {"start": v(-107.87, 70.8) * mm, "end": v(-108.45, 71.8) * mm});
            skLineSegment(sketch, "E549", {"start": v(-108.45, 71.8) * mm, "end": v(-109, 72.84) * mm});
            skLineSegment(sketch, "E550", {"start": v(-109, 72.84) * mm, "end": v(-109.54, 73.9) * mm});
            skLineSegment(sketch, "E551", {"start": v(-109.54, 73.9) * mm, "end": v(-110.04, 75) * mm});
            skLineSegment(sketch, "E552", {"start": v(-110.04, 75) * mm, "end": v(-110.53, 76.1) * mm});
            skLineSegment(sketch, "E553", {"start": v(-110.53, 76.1) * mm, "end": v(-110.99, 77.24) * mm});
            skLineSegment(sketch, "E554", {"start": v(-110.99, 77.24) * mm, "end": v(-106.02, 82.4) * mm});
            skLineSegment(sketch, "E555", {"start": v(-106.02, 82.4) * mm, "end": v(-104.87, 81.98) * mm});
            skLineSegment(sketch, "E556", {"start": v(-104.87, 81.98) * mm, "end": v(-103.74, 81.54) * mm});
            skLineSegment(sketch, "E557", {"start": v(-103.74, 81.54) * mm, "end": v(-102.63, 81.08) * mm});
            skLineSegment(sketch, "E558", {"start": v(-102.63, 81.08) * mm, "end": v(-101.55, 80.59) * mm});
            skLineSegment(sketch, "E559", {"start": v(-101.55, 80.59) * mm, "end": v(-100.49, 80.07) * mm});
            skLineSegment(sketch, "E560", {"start": v(-100.49, 80.07) * mm, "end": v(-99.46, 79.52) * mm});
            skLineSegment(sketch, "E561", {"start": v(-99.46, 79.52) * mm, "end": v(-98.46, 78.95) * mm});
            skLineSegment(sketch, "E562", {"start": v(-98.46, 78.95) * mm, "end": v(-97.49, 78.34) * mm});
            skLineSegment(sketch, "E563", {"start": v(-97.49, 78.34) * mm, "end": v(-97.02, 78.03) * mm});
            skLineSegment(sketch, "E564", {"start": v(-97.02, 78.03) * mm, "end": v(-96.55, 77.7) * mm});
            skLineSegment(sketch, "E565", {"start": v(-96.55, 77.7) * mm, "end": v(-96.33, 77.54) * mm});
            skLineSegment(sketch, "E566", {"start": v(-96.33, 77.54) * mm, "end": v(-96.1, 77.37) * mm});
            skLineSegment(sketch, "E567", {"start": v(-96.1, 77.37) * mm, "end": v(-95.88, 77.2) * mm});
            skLineSegment(sketch, "E568", {"start": v(-95.88, 77.2) * mm, "end": v(-95.67, 77.02) * mm});
            skLineSegment(sketch, "E569", {"start": v(-95.67, 77.02) * mm, "end": v(-89.54, 82.18) * mm});
            skLineSegment(sketch, "E570", {"start": v(-89.54, 82.18) * mm, "end": v(-89.67, 82.43) * mm});
            skLineSegment(sketch, "E571", {"start": v(-89.67, 82.43) * mm, "end": v(-89.8, 82.67) * mm});
            skLineSegment(sketch, "E572", {"start": v(-89.8, 82.67) * mm, "end": v(-89.93, 82.92) * mm});
            skLineSegment(sketch, "E573", {"start": v(-89.93, 82.92) * mm, "end": v(-90.05, 83.17) * mm});
            skLineSegment(sketch, "E574", {"start": v(-90.05, 83.17) * mm, "end": v(-90.3, 83.68) * mm});
            skLineSegment(sketch, "E575", {"start": v(-90.3, 83.68) * mm, "end": v(-90.53, 84.2) * mm});
            skLineSegment(sketch, "E576", {"start": v(-90.53, 84.2) * mm, "end": v(-90.96, 85.26) * mm});
            skLineSegment(sketch, "E577", {"start": v(-90.96, 85.26) * mm, "end": v(-91.35, 86.35) * mm});
            skLineSegment(sketch, "E578", {"start": v(-91.35, 86.35) * mm, "end": v(-91.71, 87.46) * mm});
            skLineSegment(sketch, "E579", {"start": v(-91.71, 87.46) * mm, "end": v(-92.04, 88.59) * mm});
            skLineSegment(sketch, "E580", {"start": v(-92.04, 88.59) * mm, "end": v(-92.34, 89.74) * mm});
            skLineSegment(sketch, "E581", {"start": v(-92.34, 89.74) * mm, "end": v(-92.6, 90.91) * mm});
            skLineSegment(sketch, "E582", {"start": v(-92.6, 90.91) * mm, "end": v(-92.85, 92.1) * mm});
            skLineSegment(sketch, "E583", {"start": v(-92.85, 92.1) * mm, "end": v(-93.06, 93.3) * mm});
            skLineSegment(sketch, "E584", {"start": v(-93.06, 93.3) * mm, "end": v(-87.13, 97.32) * mm});
            skLineSegment(sketch, "E585", {"start": v(-87.13, 97.32) * mm, "end": v(-86.1, 96.67) * mm});
            skLineSegment(sketch, "E586", {"start": v(-86.1, 96.67) * mm, "end": v(-85.08, 96) * mm});
            skLineSegment(sketch, "E587", {"start": v(-85.08, 96) * mm, "end": v(-84.1, 95.32) * mm});
            skLineSegment(sketch, "E588", {"start": v(-84.1, 95.32) * mm, "end": v(-83.13, 94.61) * mm});
            skLineSegment(sketch, "E589", {"start": v(-83.13, 94.61) * mm, "end": v(-82.2, 93.89) * mm});
            skLineSegment(sketch, "E590", {"start": v(-82.2, 93.89) * mm, "end": v(-81.31, 93.14) * mm});
            skLineSegment(sketch, "E591", {"start": v(-81.31, 93.14) * mm, "end": v(-80.45, 92.37) * mm});
            skLineSegment(sketch, "E592", {"start": v(-80.45, 92.37) * mm, "end": v(-79.63, 91.58) * mm});
            skLineSegment(sketch, "E593", {"start": v(-79.63, 91.58) * mm, "end": v(-79.23, 91.17) * mm});
            skLineSegment(sketch, "E594", {"start": v(-79.23, 91.17) * mm, "end": v(-78.85, 90.76) * mm});
            skLineSegment(sketch, "E595", {"start": v(-78.85, 90.76) * mm, "end": v(-78.66, 90.55) * mm});
            skLineSegment(sketch, "E596", {"start": v(-78.66, 90.55) * mm, "end": v(-78.48, 90.33) * mm});
            skLineSegment(sketch, "E597", {"start": v(-78.48, 90.33) * mm, "end": v(-78.3, 90.12) * mm});
            skLineSegment(sketch, "E598", {"start": v(-78.3, 90.12) * mm, "end": v(-78.12, 89.9) * mm});
            skLineSegment(sketch, "E599", {"start": v(-78.12, 89.9) * mm, "end": v(-71.05, 93.68) * mm});
            skLineSegment(sketch, "E600", {"start": v(-71.05, 93.68) * mm, "end": v(-71.13, 93.94) * mm});
            skLineSegment(sketch, "E601", {"start": v(-71.13, 93.94) * mm, "end": v(-71.21, 94.21) * mm});
            skLineSegment(sketch, "E602", {"start": v(-71.21, 94.21) * mm, "end": v(-71.28, 94.48) * mm});
            skLineSegment(sketch, "E603", {"start": v(-71.28, 94.48) * mm, "end": v(-71.35, 94.75) * mm});
            skLineSegment(sketch, "E604", {"start": v(-71.35, 94.75) * mm, "end": v(-71.48, 95.3) * mm});
            skLineSegment(sketch, "E605", {"start": v(-71.48, 95.3) * mm, "end": v(-71.6, 95.86) * mm});
            skLineSegment(sketch, "E606", {"start": v(-71.6, 95.86) * mm, "end": v(-71.8, 96.98) * mm});
            skLineSegment(sketch, "E607", {"start": v(-71.8, 96.98) * mm, "end": v(-71.96, 98.13) * mm});
            skLineSegment(sketch, "E608", {"start": v(-71.96, 98.13) * mm, "end": v(-72.08, 99.29) * mm});
            skLineSegment(sketch, "E609", {"start": v(-72.08, 99.29) * mm, "end": v(-72.17, 100.46) * mm});
            skLineSegment(sketch, "E610", {"start": v(-72.17, 100.46) * mm, "end": v(-72.22, 101.65) * mm});
            skLineSegment(sketch, "E611", {"start": v(-72.22, 101.65) * mm, "end": v(-72.24, 102.85) * mm});
            skLineSegment(sketch, "E612", {"start": v(-72.24, 102.85) * mm, "end": v(-72.23, 104.06) * mm});
            skLineSegment(sketch, "E613", {"start": v(-72.23, 104.06) * mm, "end": v(-72.19, 105.29) * mm});
            skLineSegment(sketch, "E614", {"start": v(-72.19, 105.29) * mm, "end": v(-65.56, 107.98) * mm});
            skLineSegment(sketch, "E615", {"start": v(-65.56, 107.98) * mm, "end": v(-64.67, 107.13) * mm});
            skLineSegment(sketch, "E616", {"start": v(-64.67, 107.13) * mm, "end": v(-63.82, 106.27) * mm});
            skLineSegment(sketch, "E617", {"start": v(-63.82, 106.27) * mm, "end": v(-63, 105.4) * mm});
            skLineSegment(sketch, "E618", {"start": v(-63, 105.4) * mm, "end": v(-62.2, 104.5) * mm});
            skLineSegment(sketch, "E619", {"start": v(-62.2, 104.5) * mm, "end": v(-61.45, 103.6) * mm});
            skLineSegment(sketch, "E620", {"start": v(-61.45, 103.6) * mm, "end": v(-60.73, 102.68) * mm});
            skLineSegment(sketch, "E621", {"start": v(-60.73, 102.68) * mm, "end": v(-60.05, 101.75) * mm});
            skLineSegment(sketch, "E622", {"start": v(-60.05, 101.75) * mm, "end": v(-59.4, 100.8) * mm});
            skLineSegment(sketch, "E623", {"start": v(-59.4, 100.8) * mm, "end": v(-59.1, 100.32) * mm});
            skLineSegment(sketch, "E624", {"start": v(-59.1, 100.32) * mm, "end": v(-58.82, 99.84) * mm});
            skLineSegment(sketch, "E625", {"start": v(-58.82, 99.84) * mm, "end": v(-58.68, 99.6) * mm});
            skLineSegment(sketch, "E626", {"start": v(-58.68, 99.6) * mm, "end": v(-58.54, 99.35) * mm});
            skLineSegment(sketch, "E627", {"start": v(-58.54, 99.35) * mm, "end": v(-58.4, 99.1) * mm});
            skLineSegment(sketch, "E628", {"start": v(-58.4, 99.1) * mm, "end": v(-58.28, 98.86) * mm});
            skLineSegment(sketch, "E629", {"start": v(-58.28, 98.86) * mm, "end": v(-50.58, 101.08) * mm});
            skLineSegment(sketch, "E630", {"start": v(-50.58, 101.08) * mm, "end": v(-50.6, 101.35) * mm});
            skLineSegment(sketch, "E631", {"start": v(-50.6, 101.35) * mm, "end": v(-50.63, 101.63) * mm});
            skLineSegment(sketch, "E632", {"start": v(-50.63, 101.63) * mm, "end": v(-50.64, 101.91) * mm});
            skLineSegment(sketch, "E633", {"start": v(-50.64, 101.91) * mm, "end": v(-50.65, 102.2) * mm});
            skLineSegment(sketch, "E634", {"start": v(-50.65, 102.2) * mm, "end": v(-50.67, 102.76) * mm});
            skLineSegment(sketch, "E635", {"start": v(-50.67, 102.76) * mm, "end": v(-50.67, 103.32) * mm});
            skLineSegment(sketch, "E636", {"start": v(-50.67, 103.32) * mm, "end": v(-50.63, 104.47) * mm});
            skLineSegment(sketch, "E637", {"start": v(-50.63, 104.47) * mm, "end": v(-50.55, 105.62) * mm});
            skLineSegment(sketch, "E638", {"start": v(-50.55, 105.62) * mm, "end": v(-50.42, 106.78) * mm});
            skLineSegment(sketch, "E639", {"start": v(-50.42, 106.78) * mm, "end": v(-50.26, 107.94) * mm});
            skLineSegment(sketch, "E640", {"start": v(-50.26, 107.94) * mm, "end": v(-50.07, 109.12) * mm});
            skLineSegment(sketch, "E641", {"start": v(-50.07, 109.12) * mm, "end": v(-49.84, 110.3) * mm});
            skLineSegment(sketch, "E642", {"start": v(-49.84, 110.3) * mm, "end": v(-49.58, 111.48) * mm});
            skLineSegment(sketch, "E643", {"start": v(-49.58, 111.48) * mm, "end": v(-49.28, 112.67) * mm});
            skLineSegment(sketch, "E644", {"start": v(-49.28, 112.67) * mm, "end": v(-42.23, 113.92) * mm});
            skLineSegment(sketch, "E645", {"start": v(-42.23, 113.92) * mm, "end": v(-41.55, 112.9) * mm});
            skLineSegment(sketch, "E646", {"start": v(-41.55, 112.9) * mm, "end": v(-40.9, 111.89) * mm});
            skLineSegment(sketch, "E647", {"start": v(-40.9, 111.89) * mm, "end": v(-40.27, 110.86) * mm});
            skLineSegment(sketch, "E648", {"start": v(-40.27, 110.86) * mm, "end": v(-39.68, 109.83) * mm});
            skLineSegment(sketch, "E649", {"start": v(-39.68, 109.83) * mm, "end": v(-39.13, 108.79) * mm});
            skLineSegment(sketch, "E650", {"start": v(-39.13, 108.79) * mm, "end": v(-38.61, 107.74) * mm});
            skLineSegment(sketch, "E651", {"start": v(-38.61, 107.74) * mm, "end": v(-38.14, 106.69) * mm});
            skLineSegment(sketch, "E652", {"start": v(-38.14, 106.69) * mm, "end": v(-37.71, 105.63) * mm});
            skLineSegment(sketch, "E653", {"start": v(-37.71, 105.63) * mm, "end": v(-37.52, 105.1) * mm});
            skLineSegment(sketch, "E654", {"start": v(-37.52, 105.1) * mm, "end": v(-37.33, 104.56) * mm});
            skLineSegment(sketch, "E655", {"start": v(-37.33, 104.56) * mm, "end": v(-37.25, 104.3) * mm});
            skLineSegment(sketch, "E656", {"start": v(-37.25, 104.3) * mm, "end": v(-37.17, 104.03) * mm});
            skLineSegment(sketch, "E657", {"start": v(-37.17, 104.03) * mm, "end": v(-37.09, 103.76) * mm});
            skLineSegment(sketch, "E658", {"start": v(-37.09, 103.76) * mm, "end": v(-37.01, 103.49) * mm});
            skLineSegment(sketch, "E659", {"start": v(-37.01, 103.49) * mm, "end": v(-29.02, 104.06) * mm});
            skLineSegment(sketch, "E660", {"start": v(-29.02, 104.06) * mm, "end": v(-28.99, 104.33) * mm});
            skLineSegment(sketch, "E661", {"start": v(-28.99, 104.33) * mm, "end": v(-28.95, 104.61) * mm});
            skLineSegment(sketch, "E662", {"start": v(-28.95, 104.61) * mm, "end": v(-28.9, 104.89) * mm});
            skLineSegment(sketch, "E663", {"start": v(-28.9, 104.89) * mm, "end": v(-28.86, 105.17) * mm});
            skLineSegment(sketch, "E664", {"start": v(-28.86, 105.17) * mm, "end": v(-28.75, 105.72) * mm});
            skLineSegment(sketch, "E665", {"start": v(-28.75, 105.72) * mm, "end": v(-28.64, 106.27) * mm});
            skLineSegment(sketch, "E666", {"start": v(-28.64, 106.27) * mm, "end": v(-28.36, 107.38) * mm});
            skLineSegment(sketch, "E667", {"start": v(-28.36, 107.38) * mm, "end": v(-28.04, 108.5) * mm});
            skLineSegment(sketch, "E668", {"start": v(-28.04, 108.5) * mm, "end": v(-27.68, 109.6) * mm});
            skLineSegment(sketch, "E669", {"start": v(-27.68, 109.6) * mm, "end": v(-27.28, 110.71) * mm});
            skLineSegment(sketch, "E670", {"start": v(-27.28, 110.71) * mm, "end": v(-26.85, 111.82) * mm});
            skLineSegment(sketch, "E671", {"start": v(-26.85, 111.82) * mm, "end": v(-26.38, 112.92) * mm});
            skLineSegment(sketch, "E672", {"start": v(-26.38, 112.92) * mm, "end": v(-25.87, 114.03) * mm});
            skLineSegment(sketch, "E673", {"start": v(-25.87, 114.03) * mm, "end": v(-25.34, 115.13) * mm});
            skLineSegment(sketch, "E674", {"start": v(-25.34, 115.13) * mm, "end": v(-18.18, 114.89) * mm});
            skLineSegment(sketch, "E675", {"start": v(-18.18, 114.89) * mm, "end": v(-17.72, 113.75) * mm});
            skLineSegment(sketch, "E676", {"start": v(-17.72, 113.75) * mm, "end": v(-17.3, 112.62) * mm});
            skLineSegment(sketch, "E677", {"start": v(-17.3, 112.62) * mm, "end": v(-16.9, 111.48) * mm});
            skLineSegment(sketch, "E678", {"start": v(-16.9, 111.48) * mm, "end": v(-16.54, 110.35) * mm});
            skLineSegment(sketch, "E679", {"start": v(-16.54, 110.35) * mm, "end": v(-16.21, 109.22) * mm});
            skLineSegment(sketch, "E680", {"start": v(-16.21, 109.22) * mm, "end": v(-15.93, 108.09) * mm});
            skLineSegment(sketch, "E681", {"start": v(-15.93, 108.09) * mm, "end": v(-15.68, 106.96) * mm});
            skLineSegment(sketch, "E682", {"start": v(-15.68, 106.96) * mm, "end": v(-15.49, 105.83) * mm});
            skLineSegment(sketch, "E683", {"start": v(-15.49, 105.83) * mm, "end": v(-15.4, 105.27) * mm});
            skLineSegment(sketch, "E684", {"start": v(-15.4, 105.27) * mm, "end": v(-15.34, 104.71) * mm});
            skLineSegment(sketch, "E685", {"start": v(-15.34, 104.71) * mm, "end": v(-15.3, 104.43) * mm});
            skLineSegment(sketch, "E686", {"start": v(-15.3, 104.43) * mm, "end": v(-15.28, 104.15) * mm});
            skLineSegment(sketch, "E687", {"start": v(-15.28, 104.15) * mm, "end": v(-15.26, 103.87) * mm});
            skLineSegment(sketch, "E688", {"start": v(-15.26, 103.87) * mm, "end": v(-15.25, 103.6) * mm});
            skLineSegment(sketch, "E689", {"start": v(-15.25, 103.6) * mm, "end": v(-7.31, 102.5) * mm});
            skLineSegment(sketch, "E690", {"start": v(-7.31, 102.5) * mm, "end": v(-7.22, 102.76) * mm});
            skLineSegment(sketch, "E691", {"start": v(-7.22, 102.76) * mm, "end": v(-7.13, 103.02) * mm});
            skLineSegment(sketch, "E692", {"start": v(-7.13, 103.02) * mm, "end": v(-7.03, 103.28) * mm});
            skLineSegment(sketch, "E693", {"start": v(-7.03, 103.28) * mm, "end": v(-6.92, 103.54) * mm});
            skLineSegment(sketch, "E694", {"start": v(-6.92, 103.54) * mm, "end": v(-6.7, 104.06) * mm});
            skLineSegment(sketch, "E695", {"start": v(-6.7, 104.06) * mm, "end": v(-6.47, 104.58) * mm});
            skLineSegment(sketch, "E696", {"start": v(-6.47, 104.58) * mm, "end": v(-5.98, 105.6) * mm});
            skLineSegment(sketch, "E697", {"start": v(-5.98, 105.6) * mm, "end": v(-5.43, 106.63) * mm});
            skLineSegment(sketch, "E698", {"start": v(-5.43, 106.63) * mm, "end": v(-4.85, 107.64) * mm});
            skLineSegment(sketch, "E699", {"start": v(-4.85, 107.64) * mm, "end": v(-4.23, 108.64) * mm});
            skLineSegment(sketch, "E700", {"start": v(-4.23, 108.64) * mm, "end": v(-3.57, 109.63) * mm});
            skLineSegment(sketch, "E701", {"start": v(-3.57, 109.63) * mm, "end": v(-2.88, 110.61) * mm});
            skLineSegment(sketch, "E702", {"start": v(-2.88, 110.61) * mm, "end": v(-2.16, 111.59) * mm});
            skLineSegment(sketch, "E703", {"start": v(-2.16, 111.59) * mm, "end": v(-1.4, 112.56) * mm});
            skLineSegment(sketch, "E704", {"start": v(-1.4, 112.56) * mm, "end": v(5.54, 110.83) * mm});
            skLineSegment(sketch, "E705", {"start": v(5.54, 110.83) * mm, "end": v(5.76, 109.63) * mm});
            skLineSegment(sketch, "E706", {"start": v(5.76, 109.63) * mm, "end": v(5.94, 108.43) * mm});
            skLineSegment(sketch, "E707", {"start": v(5.94, 108.43) * mm, "end": v(6.09, 107.24) * mm});
            skLineSegment(sketch, "E708", {"start": v(6.09, 107.24) * mm, "end": v(6.2, 106.05) * mm});
            skLineSegment(sketch, "E709", {"start": v(6.2, 106.05) * mm, "end": v(6.29, 104.88) * mm});
            skLineSegment(sketch, "E710", {"start": v(6.29, 104.88) * mm, "end": v(6.33, 103.71) * mm});
            skLineSegment(sketch, "E711", {"start": v(6.33, 103.71) * mm, "end": v(6.34, 102.56) * mm});
            skLineSegment(sketch, "E712", {"start": v(6.34, 102.56) * mm, "end": v(6.3, 101.41) * mm});
            skLineSegment(sketch, "E713", {"start": v(6.3, 101.41) * mm, "end": v(6.26, 100.85) * mm});
            skLineSegment(sketch, "E714", {"start": v(6.26, 100.85) * mm, "end": v(6.2, 100.29) * mm});
            skLineSegment(sketch, "E715", {"start": v(6.2, 100.29) * mm, "end": v(6.18, 100) * mm});
            skLineSegment(sketch, "E716", {"start": v(6.18, 100) * mm, "end": v(6.14, 99.73) * mm});
            skLineSegment(sketch, "E717", {"start": v(6.14, 99.73) * mm, "end": v(6.1, 99.45) * mm});
            skLineSegment(sketch, "E718", {"start": v(6.1, 99.45) * mm, "end": v(6.06, 99.18) * mm});
            skLineSegment(sketch, "E719", {"start": v(6.06, 99.18) * mm, "end": v(13.6, 96.45) * mm});
            skLineSegment(sketch, "E720", {"start": v(13.6, 96.45) * mm, "end": v(13.74, 96.69) * mm});
            skLineSegment(sketch, "E721", {"start": v(13.74, 96.69) * mm, "end": v(13.89, 96.92) * mm});
            skLineSegment(sketch, "E722", {"start": v(13.89, 96.92) * mm, "end": v(14.04, 97.16) * mm});
            skLineSegment(sketch, "E723", {"start": v(14.04, 97.16) * mm, "end": v(14.2, 97.4) * mm});
            skLineSegment(sketch, "E724", {"start": v(14.2, 97.4) * mm, "end": v(14.52, 97.86) * mm});
            skLineSegment(sketch, "E725", {"start": v(14.52, 97.86) * mm, "end": v(14.85, 98.31) * mm});
            skLineSegment(sketch, "E726", {"start": v(14.85, 98.31) * mm, "end": v(15.55, 99.22) * mm});
            skLineSegment(sketch, "E727", {"start": v(15.55, 99.22) * mm, "end": v(16.3, 100.1) * mm});
            skLineSegment(sketch, "E728", {"start": v(16.3, 100.1) * mm, "end": v(17.08, 100.97) * mm});
            skLineSegment(sketch, "E729", {"start": v(17.08, 100.97) * mm, "end": v(17.9, 101.82) * mm});
            skLineSegment(sketch, "E730", {"start": v(17.9, 101.82) * mm, "end": v(18.74, 102.65) * mm});
            skLineSegment(sketch, "E731", {"start": v(18.74, 102.65) * mm, "end": v(19.62, 103.47) * mm});
            skLineSegment(sketch, "E732", {"start": v(19.62, 103.47) * mm, "end": v(20.53, 104.27) * mm});
            skLineSegment(sketch, "E733", {"start": v(20.53, 104.27) * mm, "end": v(21.47, 105.06) * mm});
            skLineSegment(sketch, "E734", {"start": v(21.47, 105.06) * mm, "end": v(27.9, 101.93) * mm});
            skLineSegment(sketch, "E735", {"start": v(27.9, 101.93) * mm, "end": v(27.86, 100.7) * mm});
            skLineSegment(sketch, "E736", {"start": v(27.86, 100.7) * mm, "end": v(27.8, 99.5) * mm});
            skLineSegment(sketch, "E737", {"start": v(27.8, 99.5) * mm, "end": v(27.7, 98.3) * mm});
            skLineSegment(sketch, "E738", {"start": v(27.7, 98.3) * mm, "end": v(27.56, 97.12) * mm});
            skLineSegment(sketch, "E739", {"start": v(27.56, 97.12) * mm, "end": v(27.4, 95.95) * mm});
            skLineSegment(sketch, "E740", {"start": v(27.4, 95.95) * mm, "end": v(27.2, 94.8) * mm});
            skLineSegment(sketch, "E741", {"start": v(27.2, 94.8) * mm, "end": v(26.96, 93.67) * mm});
            skLineSegment(sketch, "E742", {"start": v(26.96, 93.67) * mm, "end": v(26.68, 92.56) * mm});
            skLineSegment(sketch, "E743", {"start": v(26.68, 92.56) * mm, "end": v(26.53, 92.02) * mm});
            skLineSegment(sketch, "E744", {"start": v(26.53, 92.02) * mm, "end": v(26.36, 91.48) * mm});
            skLineSegment(sketch, "E745", {"start": v(26.36, 91.48) * mm, "end": v(26.28, 91.21) * mm});
            skLineSegment(sketch, "E746", {"start": v(26.28, 91.21) * mm, "end": v(26.19, 90.95) * mm});
            skLineSegment(sketch, "E747", {"start": v(26.19, 90.95) * mm, "end": v(26.1, 90.68) * mm});
            skLineSegment(sketch, "E748", {"start": v(26.1, 90.68) * mm, "end": v(26, 90.42) * mm});
            skLineSegment(sketch, "E749", {"start": v(26, 90.42) * mm, "end": v(32.8, 86.19) * mm});
            skLineSegment(sketch, "E750", {"start": v(32.8, 86.19) * mm, "end": v(32.98, 86.4) * mm});
            skLineSegment(sketch, "E751", {"start": v(32.98, 86.4) * mm, "end": v(33.18, 86.6) * mm});
            skLineSegment(sketch, "E752", {"start": v(33.18, 86.6) * mm, "end": v(33.37, 86.8) * mm});
            skLineSegment(sketch, "E753", {"start": v(33.37, 86.8) * mm, "end": v(33.57, 86.99) * mm});
            skLineSegment(sketch, "E754", {"start": v(33.57, 86.99) * mm, "end": v(33.99, 87.37) * mm});
            skLineSegment(sketch, "E755", {"start": v(33.99, 87.37) * mm, "end": v(34.4, 87.75) * mm});
            skLineSegment(sketch, "E756", {"start": v(34.4, 87.75) * mm, "end": v(35.28, 88.49) * mm});
            skLineSegment(sketch, "E757", {"start": v(35.28, 88.49) * mm, "end": v(36.2, 89.2) * mm});
            skLineSegment(sketch, "E758", {"start": v(36.2, 89.2) * mm, "end": v(37.14, 89.88) * mm});
            skLineSegment(sketch, "E759", {"start": v(37.14, 89.88) * mm, "end": v(38.1, 90.55) * mm});
            skLineSegment(sketch, "E760", {"start": v(38.1, 90.55) * mm, "end": v(39.11, 91.19) * mm});
            skLineSegment(sketch, "E761", {"start": v(39.11, 91.19) * mm, "end": v(40.14, 91.8) * mm});
            skLineSegment(sketch, "E762", {"start": v(40.14, 91.8) * mm, "end": v(41.2, 92.4) * mm});
            skLineSegment(sketch, "E763", {"start": v(41.2, 92.4) * mm, "end": v(42.28, 92.98) * mm});
            skLineSegment(sketch, "E764", {"start": v(42.28, 92.98) * mm, "end": v(47.93, 88.58) * mm});
            skLineSegment(sketch, "E765", {"start": v(47.93, 88.58) * mm, "end": v(47.63, 87.39) * mm});
            skLineSegment(sketch, "E766", {"start": v(47.63, 87.39) * mm, "end": v(47.31, 86.22) * mm});
            skLineSegment(sketch, "E767", {"start": v(47.31, 86.22) * mm, "end": v(46.97, 85.07) * mm});
            skLineSegment(sketch, "E768", {"start": v(46.97, 85.07) * mm, "end": v(46.6, 83.94) * mm});
            skLineSegment(sketch, "E769", {"start": v(46.6, 83.94) * mm, "end": v(46.19, 82.83) * mm});
            skLineSegment(sketch, "E770", {"start": v(46.19, 82.83) * mm, "end": v(45.75, 81.75) * mm});
            skLineSegment(sketch, "E771", {"start": v(45.75, 81.75) * mm, "end": v(45.29, 80.7) * mm});
            skLineSegment(sketch, "E772", {"start": v(45.29, 80.7) * mm, "end": v(44.79, 79.67) * mm});
            skLineSegment(sketch, "E773", {"start": v(44.79, 79.67) * mm, "end": v(44.52, 79.16) * mm});
            skLineSegment(sketch, "E774", {"start": v(44.52, 79.16) * mm, "end": v(44.25, 78.67) * mm});
            skLineSegment(sketch, "E775", {"start": v(44.25, 78.67) * mm, "end": v(44.1, 78.43) * mm});
            skLineSegment(sketch, "E776", {"start": v(44.1, 78.43) * mm, "end": v(43.96, 78.19) * mm});
            skLineSegment(sketch, "E777", {"start": v(43.96, 78.19) * mm, "end": v(43.81, 77.95) * mm});
            skLineSegment(sketch, "E778", {"start": v(43.81, 77.95) * mm, "end": v(43.66, 77.72) * mm});
            skLineSegment(sketch, "E779", {"start": v(43.66, 77.72) * mm, "end": v(49.44, 72.16) * mm});
            skLineSegment(sketch, "E780", {"start": v(49.44, 72.16) * mm, "end": v(49.66, 72.32) * mm});
            skLineSegment(sketch, "E781", {"start": v(49.66, 72.32) * mm, "end": v(49.9, 72.48) * mm});
            skLineSegment(sketch, "E782", {"start": v(49.9, 72.48) * mm, "end": v(50.13, 72.63) * mm});
            skLineSegment(sketch, "E783", {"start": v(50.13, 72.63) * mm, "end": v(50.37, 72.78) * mm});
            skLineSegment(sketch, "E784", {"start": v(50.37, 72.78) * mm, "end": v(50.85, 73.07) * mm});
            skLineSegment(sketch, "E785", {"start": v(50.85, 73.07) * mm, "end": v(51.34, 73.36) * mm});
            skLineSegment(sketch, "E786", {"start": v(51.34, 73.36) * mm, "end": v(52.35, 73.9) * mm});
            skLineSegment(sketch, "E787", {"start": v(52.35, 73.9) * mm, "end": v(53.39, 74.4) * mm});
            skLineSegment(sketch, "E788", {"start": v(53.39, 74.4) * mm, "end": v(54.45, 74.87) * mm});
            skLineSegment(sketch, "E789", {"start": v(54.45, 74.87) * mm, "end": v(55.54, 75.32) * mm});
            skLineSegment(sketch, "E790", {"start": v(55.54, 75.32) * mm, "end": v(56.66, 75.74) * mm});
            skLineSegment(sketch, "E791", {"start": v(56.66, 75.74) * mm, "end": v(57.8, 76.13) * mm});
            skLineSegment(sketch, "E792", {"start": v(57.8, 76.13) * mm, "end": v(58.95, 76.5) * mm});
            skLineSegment(sketch, "E793", {"start": v(58.95, 76.5) * mm, "end": v(60.13, 76.83) * mm});
            skLineSegment(sketch, "E794", {"start": v(60.13, 76.83) * mm, "end": v(64.74, 71.35) * mm});
            skLineSegment(sketch, "E795", {"start": v(64.74, 71.35) * mm, "end": v(64.2, 70.25) * mm});
            skLineSegment(sketch, "E796", {"start": v(64.2, 70.25) * mm, "end": v(63.65, 69.17) * mm});
            skLineSegment(sketch, "E797", {"start": v(63.65, 69.17) * mm, "end": v(63.07, 68.12) * mm});
            skLineSegment(sketch, "E798", {"start": v(63.07, 68.12) * mm, "end": v(62.46, 67.1) * mm});
            skLineSegment(sketch, "E799", {"start": v(62.46, 67.1) * mm, "end": v(61.84, 66.1) * mm});
            skLineSegment(sketch, "E800", {"start": v(61.84, 66.1) * mm, "end": v(61.2, 65.13) * mm});
            skLineSegment(sketch, "E801", {"start": v(61.2, 65.13) * mm, "end": v(60.51, 64.19) * mm});
            skLineSegment(sketch, "E802", {"start": v(60.51, 64.19) * mm, "end": v(59.81, 63.29) * mm});
            skLineSegment(sketch, "E803", {"start": v(59.81, 63.29) * mm, "end": v(59.45, 62.85) * mm});
            skLineSegment(sketch, "E804", {"start": v(59.45, 62.85) * mm, "end": v(59.08, 62.43) * mm});
            skLineSegment(sketch, "E805", {"start": v(59.08, 62.43) * mm, "end": v(58.89, 62.22) * mm});
            skLineSegment(sketch, "E806", {"start": v(58.89, 62.22) * mm, "end": v(58.7, 62.01) * mm});
            skLineSegment(sketch, "E807", {"start": v(58.7, 62.01) * mm, "end": v(58.5, 61.81) * mm});
            skLineSegment(sketch, "E808", {"start": v(58.5, 61.81) * mm, "end": v(58.3, 61.62) * mm});
            skLineSegment(sketch, "E809", {"start": v(58.3, 61.62) * mm, "end": v(62.8, 54.98) * mm});
            skLineSegment(sketch, "E810", {"start": v(62.8, 54.98) * mm, "end": v(63.05, 55.09) * mm});
            skLineSegment(sketch, "E811", {"start": v(63.05, 55.09) * mm, "end": v(63.31, 55.2) * mm});
            skLineSegment(sketch, "E812", {"start": v(63.31, 55.2) * mm, "end": v(63.57, 55.3) * mm});
            skLineSegment(sketch, "E813", {"start": v(63.57, 55.3) * mm, "end": v(63.84, 55.4) * mm});
            skLineSegment(sketch, "E814", {"start": v(63.84, 55.4) * mm, "end": v(64.37, 55.58) * mm});
            skLineSegment(sketch, "E815", {"start": v(64.37, 55.58) * mm, "end": v(64.91, 55.75) * mm});
            skLineSegment(sketch, "E816", {"start": v(64.91, 55.75) * mm, "end": v(66, 56.07) * mm});
            skLineSegment(sketch, "E817", {"start": v(66, 56.07) * mm, "end": v(67.13, 56.35) * mm});
            skLineSegment(sketch, "E818", {"start": v(67.13, 56.35) * mm, "end": v(68.27, 56.6) * mm});
            skLineSegment(sketch, "E819", {"start": v(68.27, 56.6) * mm, "end": v(69.43, 56.8) * mm});
            skLineSegment(sketch, "E820", {"start": v(69.43, 56.8) * mm, "end": v(70.6, 56.98) * mm});
            skLineSegment(sketch, "E821", {"start": v(70.6, 56.98) * mm, "end": v(71.8, 57.12) * mm});
            skLineSegment(sketch, "E822", {"start": v(71.8, 57.12) * mm, "end": v(73, 57.24) * mm});
            skLineSegment(sketch, "E823", {"start": v(73, 57.24) * mm, "end": v(74.23, 57.32) * mm});
            skLineSegment(sketch, "E824", {"start": v(74.23, 57.32) * mm, "end": v(77.6, 51) * mm});
            skLineSegment(sketch, "E825", {"start": v(77.6, 51) * mm, "end": v(76.84, 50.04) * mm});
            skLineSegment(sketch, "E826", {"start": v(76.84, 50.04) * mm, "end": v(76.08, 49.1) * mm});
            skLineSegment(sketch, "E827", {"start": v(76.08, 49.1) * mm, "end": v(75.3, 48.2) * mm});
            skLineSegment(sketch, "E828", {"start": v(75.3, 48.2) * mm, "end": v(74.49, 47.31) * mm});
            skLineSegment(sketch, "E829", {"start": v(74.49, 47.31) * mm, "end": v(73.67, 46.47) * mm});
            skLineSegment(sketch, "E830", {"start": v(73.67, 46.47) * mm, "end": v(72.83, 45.65) * mm});
            skLineSegment(sketch, "E831", {"start": v(72.83, 45.65) * mm, "end": v(71.98, 44.88) * mm});
            skLineSegment(sketch, "E832", {"start": v(71.98, 44.88) * mm, "end": v(71.1, 44.14) * mm});
            skLineSegment(sketch, "E833", {"start": v(71.1, 44.14) * mm, "end": v(70.66, 43.8) * mm});
            skLineSegment(sketch, "E834", {"start": v(70.66, 43.8) * mm, "end": v(70.2, 43.45) * mm});
            skLineSegment(sketch, "E835", {"start": v(70.2, 43.45) * mm, "end": v(69.98, 43.3) * mm});
            skLineSegment(sketch, "E836", {"start": v(69.98, 43.3) * mm, "end": v(69.75, 43.13) * mm});
            skLineSegment(sketch, "E837", {"start": v(69.75, 43.13) * mm, "end": v(69.52, 42.97) * mm});
            skLineSegment(sketch, "E838", {"start": v(69.52, 42.97) * mm, "end": v(69.28, 42.82) * mm});
            skLineSegment(sketch, "E839", {"start": v(69.28, 42.82) * mm, "end": v(72.3, 35.4) * mm});
            skLineSegment(sketch, "E840", {"start": v(72.3, 35.4) * mm, "end": v(72.57, 35.45) * mm});
            skLineSegment(sketch, "E841", {"start": v(72.57, 35.45) * mm, "end": v(72.85, 35.5) * mm});
            skLineSegment(sketch, "E842", {"start": v(72.85, 35.5) * mm, "end": v(73.12, 35.54) * mm});
            skLineSegment(sketch, "E843", {"start": v(73.12, 35.54) * mm, "end": v(73.4, 35.58) * mm});
            skLineSegment(sketch, "E844", {"start": v(73.4, 35.58) * mm, "end": v(73.96, 35.65) * mm});
            skLineSegment(sketch, "E845", {"start": v(73.96, 35.65) * mm, "end": v(74.52, 35.71) * mm});
            skLineSegment(sketch, "E846", {"start": v(74.52, 35.71) * mm, "end": v(75.66, 35.8) * mm});
            skLineSegment(sketch, "E847", {"start": v(75.66, 35.8) * mm, "end": v(76.82, 35.83) * mm});
            skLineSegment(sketch, "E848", {"start": v(76.82, 35.83) * mm, "end": v(77.98, 35.83) * mm});
            skLineSegment(sketch, "E849", {"start": v(77.98, 35.83) * mm, "end": v(79.16, 35.8) * mm});
            skLineSegment(sketch, "E850", {"start": v(79.16, 35.8) * mm, "end": v(80.35, 35.73) * mm});
            skLineSegment(sketch, "E851", {"start": v(80.35, 35.73) * mm, "end": v(81.55, 35.62) * mm});
            skLineSegment(sketch, "E852", {"start": v(81.55, 35.62) * mm, "end": v(82.75, 35.48) * mm});
            skLineSegment(sketch, "E853", {"start": v(82.75, 35.48) * mm, "end": v(83.96, 35.31) * mm});
            skLineSegment(sketch, "E854", {"start": v(83.96, 35.31) * mm, "end": v(85.95, 28.43) * mm});
            skLineSegment(sketch, "E855", {"start": v(85.95, 28.43) * mm, "end": v(85.01, 27.65) * mm});
            skLineSegment(sketch, "E856", {"start": v(85.01, 27.65) * mm, "end": v(84.06, 26.89) * mm});
            skLineSegment(sketch, "E857", {"start": v(84.06, 26.89) * mm, "end": v(83.1, 26.16) * mm});
            skLineSegment(sketch, "E858", {"start": v(83.1, 26.16) * mm, "end": v(82.14, 25.47) * mm});
            skLineSegment(sketch, "E859", {"start": v(82.14, 25.47) * mm, "end": v(81.16, 24.8) * mm});
            skLineSegment(sketch, "E860", {"start": v(81.16, 24.8) * mm, "end": v(80.17, 24.19) * mm});
            skLineSegment(sketch, "E861", {"start": v(80.17, 24.19) * mm, "end": v(79.18, 23.6) * mm});
            skLineSegment(sketch, "E862", {"start": v(79.18, 23.6) * mm, "end": v(78.17, 23.07) * mm});
            skLineSegment(sketch, "E863", {"start": v(78.17, 23.07) * mm, "end": v(77.66, 22.82) * mm});
            skLineSegment(sketch, "E864", {"start": v(77.66, 22.82) * mm, "end": v(77.15, 22.58) * mm});
            skLineSegment(sketch, "E865", {"start": v(77.15, 22.58) * mm, "end": v(76.9, 22.47) * mm});
            skLineSegment(sketch, "E866", {"start": v(76.9, 22.47) * mm, "end": v(76.63, 22.36) * mm});
            skLineSegment(sketch, "E867", {"start": v(76.63, 22.36) * mm, "end": v(76.37, 22.25) * mm});
            skLineSegment(sketch, "E868", {"start": v(76.37, 22.25) * mm, "end": v(76.11, 22.15) * mm});
            skLineSegment(sketch, "E869", {"start": v(76.11, 22.15) * mm, "end": v(77.52, 14.26) * mm});
            skLineSegment(sketch, "E870", {"start": v(77.52, 14.26) * mm, "end": v(77.8, 14.26) * mm});
            skLineSegment(sketch, "E871", {"start": v(77.8, 14.26) * mm, "end": v(78.07, 14.25) * mm});
            skLineSegment(sketch, "E872", {"start": v(78.07, 14.25) * mm, "end": v(78.35, 14.24) * mm});
            skLineSegment(sketch, "E873", {"start": v(78.35, 14.24) * mm, "end": v(78.63, 14.22) * mm});
            skLineSegment(sketch, "E874", {"start": v(78.63, 14.22) * mm, "end": v(79.2, 14.17) * mm});
            skLineSegment(sketch, "E875", {"start": v(79.2, 14.17) * mm, "end": v(79.76, 14.11) * mm});
            skLineSegment(sketch, "E876", {"start": v(79.76, 14.11) * mm, "end": v(80.9, 13.96) * mm});
            skLineSegment(sketch, "E877", {"start": v(80.9, 13.96) * mm, "end": v(82.03, 13.75) * mm});
            skLineSegment(sketch, "E878", {"start": v(82.03, 13.75) * mm, "end": v(83.17, 13.51) * mm});
            skLineSegment(sketch, "E879", {"start": v(83.17, 13.51) * mm, "end": v(84.31, 13.23) * mm});
            skLineSegment(sketch, "E880", {"start": v(84.31, 13.23) * mm, "end": v(85.46, 12.91) * mm});
            skLineSegment(sketch, "E881", {"start": v(85.46, 12.91) * mm, "end": v(86.6, 12.56) * mm});
            skLineSegment(sketch, "E882", {"start": v(86.6, 12.56) * mm, "end": v(87.76, 12.18) * mm});
            skLineSegment(sketch, "E883", {"start": v(87.76, 12.18) * mm, "end": v(88.91, 11.76) * mm});
            skLineSegment(sketch, "E884", {"start": v(88.91, 11.76) * mm, "end": v(89.42, 4.62) * mm});
            skLineSegment(sketch, "E885", {"start": v(89.42, 4.62) * mm, "end": v(88.34, 4.04) * mm});
            skLineSegment(sketch, "E886", {"start": v(88.34, 4.04) * mm, "end": v(87.26, 3.5) * mm});
            skLineSegment(sketch, "E887", {"start": v(87.26, 3.5) * mm, "end": v(86.17, 2.98) * mm});
            skLineSegment(sketch, "E888", {"start": v(86.17, 2.98) * mm, "end": v(85.08, 2.5) * mm});
            skLineSegment(sketch, "E889", {"start": v(85.08, 2.5) * mm, "end": v(83.99, 2.07) * mm});
            skLineSegment(sketch, "E890", {"start": v(83.99, 2.07) * mm, "end": v(82.9, 1.66) * mm});
            skLineSegment(sketch, "E891", {"start": v(82.9, 1.66) * mm, "end": v(81.8, 1.3) * mm});
            skLineSegment(sketch, "E892", {"start": v(81.8, 1.3) * mm, "end": v(80.7, 0.99) * mm});
            skLineSegment(sketch, "E893", {"start": v(80.7, 0.99) * mm, "end": v(80.15, 0.85) * mm});
            skLineSegment(sketch, "E894", {"start": v(80.15, 0.85) * mm, "end": v(79.6, 0.72) * mm});
            skLineSegment(sketch, "E895", {"start": v(79.6, 0.72) * mm, "end": v(79.32, 0.67) * mm});
            skLineSegment(sketch, "E896", {"start": v(79.32, 0.67) * mm, "end": v(79.05, 0.61) * mm});
            skLineSegment(sketch, "E897", {"start": v(79.05, 0.61) * mm, "end": v(78.77, 0.56) * mm});
            skLineSegment(sketch, "E898", {"start": v(78.77, 0.56) * mm, "end": v(78.5, 0.52) * mm});
            skLineSegment(sketch, "E899", {"start": v(78.5, 0.52) * mm, "end": v(78.23, -7.5) * mm});
            skLineSegment(sketch, "E900", {"start": v(-22.44, 0) * mm, "end": v(-22.55, 0.82) * mm});
            skLineSegment(sketch, "E901", {"start": v(-22.55, 0.82) * mm, "end": v(-22.87, 1.59) * mm});
            skLineSegment(sketch, "E902", {"start": v(-22.87, 1.59) * mm, "end": v(-23.37, 2.24) * mm});
            skLineSegment(sketch, "E903", {"start": v(-23.37, 2.24) * mm, "end": v(-24.03, 2.75) * mm});
            skLineSegment(sketch, "E904", {"start": v(-24.03, 2.75) * mm, "end": v(-24.8, 3.07) * mm});
            skLineSegment(sketch, "E905", {"start": v(-24.8, 3.07) * mm, "end": v(-25.62, 3.17) * mm});
            skLineSegment(sketch, "E906", {"start": v(-25.62, 3.17) * mm, "end": v(-26.44, 3.07) * mm});
            skLineSegment(sketch, "E907", {"start": v(-26.44, 3.07) * mm, "end": v(-27.2, 2.75) * mm});
            skLineSegment(sketch, "E908", {"start": v(-27.2, 2.75) * mm, "end": v(-27.86, 2.24) * mm});
            skLineSegment(sketch, "E909", {"start": v(-27.86, 2.24) * mm, "end": v(-28.37, 1.59) * mm});
            skLineSegment(sketch, "E910", {"start": v(-28.37, 1.59) * mm, "end": v(-28.68, 0.82) * mm});
            skLineSegment(sketch, "E911", {"start": v(-28.68, 0.82) * mm, "end": v(-28.8, 0) * mm});
            skLineSegment(sketch, "E912", {"start": v(-28.8, 0) * mm, "end": v(-28.68, -0.82) * mm});
            skLineSegment(sketch, "E913", {"start": v(-28.68, -0.82) * mm, "end": v(-28.37, -1.59) * mm});
            skLineSegment(sketch, "E914", {"start": v(-28.37, -1.59) * mm, "end": v(-27.86, -2.24) * mm});
            skLineSegment(sketch, "E915", {"start": v(-27.86, -2.24) * mm, "end": v(-27.2, -2.75) * mm});
            skLineSegment(sketch, "E916", {"start": v(-27.2, -2.75) * mm, "end": v(-26.44, -3.07) * mm});
            skLineSegment(sketch, "E917", {"start": v(-26.44, -3.07) * mm, "end": v(-25.62, -3.18) * mm});
            skLineSegment(sketch, "E918", {"start": v(-25.62, -3.18) * mm, "end": v(-24.8, -3.07) * mm});
            skLineSegment(sketch, "E919", {"start": v(-24.8, -3.07) * mm, "end": v(-24.03, -2.75) * mm});
            skLineSegment(sketch, "E920", {"start": v(-24.03, -2.75) * mm, "end": v(-23.37, -2.24) * mm});
            skLineSegment(sketch, "E921", {"start": v(-23.37, -2.24) * mm, "end": v(-22.87, -1.59) * mm});
            skLineSegment(sketch, "E922", {"start": v(-22.87, -1.59) * mm, "end": v(-22.55, -0.82) * mm});
            skLineSegment(sketch, "E923", {"start": v(-22.55, -0.82) * mm, "end": v(-22.44, 0) * mm});
            skLineSegment(sketch, "E924", {"start": v(107.67, -7.65) * mm, "end": v(107.13, -7.2) * mm});
            skLineSegment(sketch, "E925", {"start": v(107.13, -7.2) * mm, "end": v(106.83, -7.1) * mm});
            skLineSegment(sketch, "E926", {"start": v(106.83, -7.1) * mm, "end": v(106.58, -7.04) * mm});
            skLineSegment(sketch, "E927", {"start": v(106.58, -7.04) * mm, "end": v(106.35, -7.01) * mm});
            skLineSegment(sketch, "E928", {"start": v(106.35, -7.01) * mm, "end": v(106.13, -7) * mm});
            skLineSegment(sketch, "E929", {"start": v(106.13, -7) * mm, "end": v(105.93, -7.02) * mm});
            skLineSegment(sketch, "E930", {"start": v(105.93, -7.02) * mm, "end": v(105.54, -7.09) * mm});
            skLineSegment(sketch, "E931", {"start": v(105.54, -7.09) * mm, "end": v(105.18, -7.19) * mm});
            skLineSegment(sketch, "E932", {"start": v(105.18, -7.19) * mm, "end": v(104.83, -7.32) * mm});
            skLineSegment(sketch, "E933", {"start": v(104.83, -7.32) * mm, "end": v(104.18, -7.67) * mm});
            skLineSegment(sketch, "E934", {"start": v(104.18, -7.67) * mm, "end": v(103.58, -8.1) * mm});
            skLineSegment(sketch, "E935", {"start": v(103.58, -8.1) * mm, "end": v(103.02, -8.6) * mm});
            skLineSegment(sketch, "E936", {"start": v(103.02, -8.6) * mm, "end": v(102.36, -8.93) * mm});
            skLineSegment(sketch, "E937", {"start": v(102.36, -8.93) * mm, "end": v(101.6, -9.06) * mm});
            skLineSegment(sketch, "E938", {"start": v(101.6, -9.06) * mm, "end": v(100.78, -9.1) * mm});
            skLineSegment(sketch, "E939", {"start": v(100.78, -9.1) * mm, "end": v(99.94, -9.07) * mm});
            skLineSegment(sketch, "E940", {"start": v(99.94, -9.07) * mm, "end": v(99.07, -8.97) * mm});
            skLineSegment(sketch, "E941", {"start": v(99.07, -8.97) * mm, "end": v(98.18, -8.79) * mm});
            skLineSegment(sketch, "E942", {"start": v(98.18, -8.79) * mm, "end": v(97.27, -8.54) * mm});
            skLineSegment(sketch, "E943", {"start": v(97.27, -8.54) * mm, "end": v(96.36, -8.23) * mm});
            skLineSegment(sketch, "E944", {"start": v(96.36, -8.23) * mm, "end": v(95.43, -7.84) * mm});
            skLineSegment(sketch, "E945", {"start": v(95.43, -7.84) * mm, "end": v(94.58, -4.75) * mm});
            skLineSegment(sketch, "E946", {"start": v(94.58, -4.75) * mm, "end": v(94.16, -1.57) * mm});
            skLineSegment(sketch, "E947", {"start": v(94.16, -1.57) * mm, "end": v(94.86, -0.85) * mm});
            skLineSegment(sketch, "E948", {"start": v(94.86, -0.85) * mm, "end": v(95.58, -0.2) * mm});
            skLineSegment(sketch, "E949", {"start": v(95.58, -0.2) * mm, "end": v(96.31, 0.38) * mm});
            skLineSegment(sketch, "E950", {"start": v(96.31, 0.38) * mm, "end": v(97.06, 0.89) * mm});
            skLineSegment(sketch, "E951", {"start": v(97.06, 0.89) * mm, "end": v(97.82, 1.32) * mm});
            skLineSegment(sketch, "E952", {"start": v(97.82, 1.32) * mm, "end": v(98.59, 1.68) * mm});
            skLineSegment(sketch, "E953", {"start": v(98.59, 1.68) * mm, "end": v(99.35, 1.96) * mm});
            skLineSegment(sketch, "E954", {"start": v(99.35, 1.96) * mm, "end": v(100.1, 2.14) * mm});
            skLineSegment(sketch, "E955", {"start": v(100.1, 2.14) * mm, "end": v(100.84, 2.1) * mm});
            skLineSegment(sketch, "E956", {"start": v(100.84, 2.1) * mm, "end": v(101.55, 1.85) * mm});
            skLineSegment(sketch, "E957", {"start": v(101.55, 1.85) * mm, "end": v(102.28, 1.7) * mm});
            skLineSegment(sketch, "E958", {"start": v(102.28, 1.7) * mm, "end": v(103, 1.63) * mm});
            skLineSegment(sketch, "E959", {"start": v(103, 1.63) * mm, "end": v(103.38, 1.64) * mm});
            skLineSegment(sketch, "E960", {"start": v(103.38, 1.64) * mm, "end": v(103.75, 1.7) * mm});
            skLineSegment(sketch, "E961", {"start": v(103.75, 1.7) * mm, "end": v(104.13, 1.78) * mm});
            skLineSegment(sketch, "E962", {"start": v(104.13, 1.78) * mm, "end": v(104.33, 1.85) * mm});
            skLineSegment(sketch, "E963", {"start": v(104.33, 1.85) * mm, "end": v(104.53, 1.94) * mm});
            skLineSegment(sketch, "E964", {"start": v(104.53, 1.94) * mm, "end": v(104.73, 2.05) * mm});
            skLineSegment(sketch, "E965", {"start": v(104.73, 2.05) * mm, "end": v(104.94, 2.2) * mm});
            skLineSegment(sketch, "E966", {"start": v(104.94, 2.2) * mm, "end": v(105.17, 2.42) * mm});
            skLineSegment(sketch, "E967", {"start": v(105.17, 2.42) * mm, "end": v(105.49, 3.04) * mm});
            skLineSegment(sketch, "E968", {"start": v(105.49, 3.04) * mm, "end": v(106.27, 5.29) * mm});
            skLineSegment(sketch, "E969", {"start": v(106.27, 5.29) * mm, "end": v(107.45, 7.35) * mm});
            skLineSegment(sketch, "E970", {"start": v(107.45, 7.35) * mm, "end": v(107.7, 8) * mm});
            skLineSegment(sketch, "E971", {"start": v(107.7, 8) * mm, "end": v(107.72, 8.32) * mm});
            skLineSegment(sketch, "E972", {"start": v(107.72, 8.32) * mm, "end": v(107.7, 8.57) * mm});
            skLineSegment(sketch, "E973", {"start": v(107.7, 8.57) * mm, "end": v(107.65, 8.8) * mm});
            skLineSegment(sketch, "E974", {"start": v(107.65, 8.8) * mm, "end": v(107.59, 9) * mm});
            skLineSegment(sketch, "E975", {"start": v(107.59, 9) * mm, "end": v(107.51, 9.2) * mm});
            skLineSegment(sketch, "E976", {"start": v(107.51, 9.2) * mm, "end": v(107.33, 9.55) * mm});
            skLineSegment(sketch, "E977", {"start": v(107.33, 9.55) * mm, "end": v(107.12, 9.86) * mm});
            skLineSegment(sketch, "E978", {"start": v(107.12, 9.86) * mm, "end": v(106.89, 10.15) * mm});
            skLineSegment(sketch, "E979", {"start": v(106.89, 10.15) * mm, "end": v(106.36, 10.66) * mm});
            skLineSegment(sketch, "E980", {"start": v(106.36, 10.66) * mm, "end": v(105.77, 11.1) * mm});
            skLineSegment(sketch, "E981", {"start": v(105.77, 11.1) * mm, "end": v(105.12, 11.48) * mm});
            skLineSegment(sketch, "E982", {"start": v(105.12, 11.48) * mm, "end": v(104.6, 12) * mm});
            skLineSegment(sketch, "E983", {"start": v(104.6, 12) * mm, "end": v(104.24, 12.7) * mm});
            skLineSegment(sketch, "E984", {"start": v(104.24, 12.7) * mm, "end": v(103.94, 13.45) * mm});
            skLineSegment(sketch, "E985", {"start": v(103.94, 13.45) * mm, "end": v(103.71, 14.26) * mm});
            skLineSegment(sketch, "E986", {"start": v(103.71, 14.26) * mm, "end": v(103.54, 15.12) * mm});
            skLineSegment(sketch, "E987", {"start": v(103.54, 15.12) * mm, "end": v(103.44, 16.02) * mm});
            skLineSegment(sketch, "E988", {"start": v(103.44, 16.02) * mm, "end": v(103.4, 16.96) * mm});
            skLineSegment(sketch, "E989", {"start": v(103.4, 16.96) * mm, "end": v(103.4, 17.93) * mm});
            skLineSegment(sketch, "E990", {"start": v(103.4, 17.93) * mm, "end": v(103.5, 18.93) * mm});
            skLineSegment(sketch, "E991", {"start": v(103.5, 18.93) * mm, "end": v(106.17, 20.7) * mm});
            skLineSegment(sketch, "E992", {"start": v(106.17, 20.7) * mm, "end": v(109.06, 22.08) * mm});
            skLineSegment(sketch, "E993", {"start": v(109.06, 22.08) * mm, "end": v(109.96, 21.64) * mm});
            skLineSegment(sketch, "E994", {"start": v(109.96, 21.64) * mm, "end": v(110.8, 21.15) * mm});
            skLineSegment(sketch, "E995", {"start": v(110.8, 21.15) * mm, "end": v(111.58, 20.63) * mm});
            skLineSegment(sketch, "E996", {"start": v(111.58, 20.63) * mm, "end": v(112.3, 20.08) * mm});
            skLineSegment(sketch, "E997", {"start": v(112.3, 20.08) * mm, "end": v(112.94, 19.49) * mm});
            skLineSegment(sketch, "E998", {"start": v(112.94, 19.49) * mm, "end": v(113.52, 18.87) * mm});
            skLineSegment(sketch, "E999", {"start": v(113.52, 18.87) * mm, "end": v(114.02, 18.23) * mm});
            skLineSegment(sketch, "E1000", {"start": v(114.02, 18.23) * mm, "end": v(114.43, 17.57) * mm});
            skLineSegment(sketch, "E1001", {"start": v(114.43, 17.57) * mm, "end": v(114.6, 16.85) * mm});
            skLineSegment(sketch, "E1002", {"start": v(114.6, 16.85) * mm, "end": v(114.6, 16.1) * mm});
            skLineSegment(sketch, "E1003", {"start": v(114.6, 16.1) * mm, "end": v(114.67, 15.37) * mm});
            skLineSegment(sketch, "E1004", {"start": v(114.67, 15.37) * mm, "end": v(114.84, 14.65) * mm});
            skLineSegment(sketch, "E1005", {"start": v(114.84, 14.65) * mm, "end": v(114.96, 14.3) * mm});
            skLineSegment(sketch, "E1006", {"start": v(114.96, 14.3) * mm, "end": v(115.12, 13.96) * mm});
            skLineSegment(sketch, "E1007", {"start": v(115.12, 13.96) * mm, "end": v(115.33, 13.63) * mm});
            skLineSegment(sketch, "E1008", {"start": v(115.33, 13.63) * mm, "end": v(115.46, 13.46) * mm});
            skLineSegment(sketch, "E1009", {"start": v(115.46, 13.46) * mm, "end": v(115.6, 13.3) * mm});
            skLineSegment(sketch, "E1010", {"start": v(115.6, 13.3) * mm, "end": v(115.77, 13.14) * mm});
            skLineSegment(sketch, "E1011", {"start": v(115.77, 13.14) * mm, "end": v(115.98, 13) * mm});
            skLineSegment(sketch, "E1012", {"start": v(115.98, 13) * mm, "end": v(116.26, 12.84) * mm});
            skLineSegment(sketch, "E1013", {"start": v(116.26, 12.84) * mm, "end": v(116.95, 12.73) * mm});
            skLineSegment(sketch, "E1014", {"start": v(116.95, 12.73) * mm, "end": v(119.32, 12.68) * mm});
            skLineSegment(sketch, "E1015", {"start": v(119.32, 12.68) * mm, "end": v(121.65, 12.2) * mm});
            skLineSegment(sketch, "E1016", {"start": v(121.65, 12.2) * mm, "end": v(122.35, 12.15) * mm});
            skLineSegment(sketch, "E1017", {"start": v(122.35, 12.15) * mm, "end": v(122.65, 12.23) * mm});
            skLineSegment(sketch, "E1018", {"start": v(122.65, 12.23) * mm, "end": v(122.9, 12.34) * mm});
            skLineSegment(sketch, "E1019", {"start": v(122.9, 12.34) * mm, "end": v(123.1, 12.45) * mm});
            skLineSegment(sketch, "E1020", {"start": v(123.1, 12.45) * mm, "end": v(123.27, 12.58) * mm});
            skLineSegment(sketch, "E1021", {"start": v(123.27, 12.58) * mm, "end": v(123.43, 12.7) * mm});
            skLineSegment(sketch, "E1022", {"start": v(123.43, 12.7) * mm, "end": v(123.7, 12.99) * mm});
            skLineSegment(sketch, "E1023", {"start": v(123.7, 12.99) * mm, "end": v(123.94, 13.28) * mm});
            skLineSegment(sketch, "E1024", {"start": v(123.94, 13.28) * mm, "end": v(124.14, 13.6) * mm});
            skLineSegment(sketch, "E1025", {"start": v(124.14, 13.6) * mm, "end": v(124.46, 14.26) * mm});
            skLineSegment(sketch, "E1026", {"start": v(124.46, 14.26) * mm, "end": v(124.7, 14.96) * mm});
            skLineSegment(sketch, "E1027", {"start": v(124.7, 14.96) * mm, "end": v(124.86, 15.69) * mm});
            skLineSegment(sketch, "E1028", {"start": v(124.86, 15.69) * mm, "end": v(125.2, 16.34) * mm});
            skLineSegment(sketch, "E1029", {"start": v(125.2, 16.34) * mm, "end": v(125.74, 16.9) * mm});
            skLineSegment(sketch, "E1030", {"start": v(125.74, 16.9) * mm, "end": v(126.37, 17.41) * mm});
            skLineSegment(sketch, "E1031", {"start": v(126.37, 17.41) * mm, "end": v(127.07, 17.89) * mm});
            skLineSegment(sketch, "E1032", {"start": v(127.07, 17.89) * mm, "end": v(127.83, 18.31) * mm});
            skLineSegment(sketch, "E1033", {"start": v(127.83, 18.31) * mm, "end": v(128.66, 18.7) * mm});
            skLineSegment(sketch, "E1034", {"start": v(128.66, 18.7) * mm, "end": v(129.53, 19.03) * mm});
            skLineSegment(sketch, "E1035", {"start": v(129.53, 19.03) * mm, "end": v(130.46, 19.3) * mm});
            skLineSegment(sketch, "E1036", {"start": v(130.46, 19.3) * mm, "end": v(131.44, 19.54) * mm});
            skLineSegment(sketch, "E1037", {"start": v(131.44, 19.54) * mm, "end": v(133.94, 17.54) * mm});
            skLineSegment(sketch, "E1038", {"start": v(133.94, 17.54) * mm, "end": v(136.15, 15.22) * mm});
            skLineSegment(sketch, "E1039", {"start": v(136.15, 15.22) * mm, "end": v(136.01, 14.23) * mm});
            skLineSegment(sketch, "E1040", {"start": v(136.01, 14.23) * mm, "end": v(135.81, 13.28) * mm});
            skLineSegment(sketch, "E1041", {"start": v(135.81, 13.28) * mm, "end": v(135.56, 12.37) * mm});
            skLineSegment(sketch, "E1042", {"start": v(135.56, 12.37) * mm, "end": v(135.25, 11.52) * mm});
            skLineSegment(sketch, "E1043", {"start": v(135.25, 11.52) * mm, "end": v(134.9, 10.72) * mm});
            skLineSegment(sketch, "E1044", {"start": v(134.9, 10.72) * mm, "end": v(134.49, 9.98) * mm});
            skLineSegment(sketch, "E1045", {"start": v(134.49, 9.98) * mm, "end": v(134.03, 9.3) * mm});
            skLineSegment(sketch, "E1046", {"start": v(134.03, 9.3) * mm, "end": v(133.52, 8.72) * mm});
            skLineSegment(sketch, "E1047", {"start": v(133.52, 8.72) * mm, "end": v(132.9, 8.32) * mm});
            skLineSegment(sketch, "E1048", {"start": v(132.9, 8.32) * mm, "end": v(132.18, 8.1) * mm});
            skLineSegment(sketch, "E1049", {"start": v(132.18, 8.1) * mm, "end": v(131.5, 7.8) * mm});
            skLineSegment(sketch, "E1050", {"start": v(131.5, 7.8) * mm, "end": v(130.88, 7.43) * mm});
            skLineSegment(sketch, "E1051", {"start": v(130.88, 7.43) * mm, "end": v(130.58, 7.2) * mm});
            skLineSegment(sketch, "E1052", {"start": v(130.58, 7.2) * mm, "end": v(130.3, 6.94) * mm});
            skLineSegment(sketch, "E1053", {"start": v(130.3, 6.94) * mm, "end": v(130.05, 6.64) * mm});
            skLineSegment(sketch, "E1054", {"start": v(130.05, 6.64) * mm, "end": v(129.94, 6.47) * mm});
            skLineSegment(sketch, "E1055", {"start": v(129.94, 6.47) * mm, "end": v(129.83, 6.28) * mm});
            skLineSegment(sketch, "E1056", {"start": v(129.83, 6.28) * mm, "end": v(129.73, 6.07) * mm});
            skLineSegment(sketch, "E1057", {"start": v(129.73, 6.07) * mm, "end": v(129.65, 5.83) * mm});
            skLineSegment(sketch, "E1058", {"start": v(129.65, 5.83) * mm, "end": v(129.6, 5.51) * mm});
            skLineSegment(sketch, "E1059", {"start": v(129.6, 5.51) * mm, "end": v(129.7, 4.82) * mm});
            skLineSegment(sketch, "E1060", {"start": v(129.7, 4.82) * mm, "end": v(130.39, 2.55) * mm});
            skLineSegment(sketch, "E1061", {"start": v(130.39, 2.55) * mm, "end": v(130.64, 0.19) * mm});
            skLineSegment(sketch, "E1062", {"start": v(130.64, 0.19) * mm, "end": v(130.82, -0.5) * mm});
            skLineSegment(sketch, "E1063", {"start": v(130.82, -0.5) * mm, "end": v(131, -0.76) * mm});
            skLineSegment(sketch, "E1064", {"start": v(131, -0.76) * mm, "end": v(131.16, -0.95) * mm});
            skLineSegment(sketch, "E1065", {"start": v(131.16, -0.95) * mm, "end": v(131.34, -1.1) * mm});
            skLineSegment(sketch, "E1066", {"start": v(131.34, -1.1) * mm, "end": v(131.5, -1.24) * mm});
            skLineSegment(sketch, "E1067", {"start": v(131.5, -1.24) * mm, "end": v(131.68, -1.35) * mm});
            skLineSegment(sketch, "E1068", {"start": v(131.68, -1.35) * mm, "end": v(132.03, -1.52) * mm});
            skLineSegment(sketch, "E1069", {"start": v(132.03, -1.52) * mm, "end": v(132.39, -1.65) * mm});
            skLineSegment(sketch, "E1070", {"start": v(132.39, -1.65) * mm, "end": v(132.75, -1.75) * mm});
            skLineSegment(sketch, "E1071", {"start": v(132.75, -1.75) * mm, "end": v(133.47, -1.85) * mm});
            skLineSegment(sketch, "E1072", {"start": v(133.47, -1.85) * mm, "end": v(134.21, -1.86) * mm});
            skLineSegment(sketch, "E1073", {"start": v(134.21, -1.86) * mm, "end": v(134.96, -1.78) * mm});
            skLineSegment(sketch, "E1074", {"start": v(134.96, -1.78) * mm, "end": v(135.69, -1.9) * mm});
            skLineSegment(sketch, "E1075", {"start": v(135.69, -1.9) * mm, "end": v(136.39, -2.25) * mm});
            skLineSegment(sketch, "E1076", {"start": v(136.39, -2.25) * mm, "end": v(137.07, -2.69) * mm});
            skLineSegment(sketch, "E1077", {"start": v(137.07, -2.69) * mm, "end": v(137.73, -3.2) * mm});
            skLineSegment(sketch, "E1078", {"start": v(137.73, -3.2) * mm, "end": v(138.37, -3.8) * mm});
            skLineSegment(sketch, "E1079", {"start": v(138.37, -3.8) * mm, "end": v(139, -4.47) * mm});
            skLineSegment(sketch, "E1080", {"start": v(139, -4.47) * mm, "end": v(139.58, -5.2) * mm});
            skLineSegment(sketch, "E1081", {"start": v(139.58, -5.2) * mm, "end": v(140.13, -6) * mm});
            skLineSegment(sketch, "E1082", {"start": v(140.13, -6) * mm, "end": v(140.65, -6.85) * mm});
            skLineSegment(sketch, "E1083", {"start": v(140.65, -6.85) * mm, "end": v(139.52, -9.85) * mm});
            skLineSegment(sketch, "E1084", {"start": v(139.52, -9.85) * mm, "end": v(138, -12.67) * mm});
            skLineSegment(sketch, "E1085", {"start": v(138, -12.67) * mm, "end": v(137.02, -12.84) * mm});
            skLineSegment(sketch, "E1086", {"start": v(137.02, -12.84) * mm, "end": v(136.05, -12.95) * mm});
            skLineSegment(sketch, "E1087", {"start": v(136.05, -12.95) * mm, "end": v(135.11, -12.98) * mm});
            skLineSegment(sketch, "E1088", {"start": v(135.11, -12.98) * mm, "end": v(134.2, -12.96) * mm});
            skLineSegment(sketch, "E1089", {"start": v(134.2, -12.96) * mm, "end": v(133.34, -12.86) * mm});
            skLineSegment(sketch, "E1090", {"start": v(133.34, -12.86) * mm, "end": v(132.5, -12.7) * mm});
            skLineSegment(sketch, "E1091", {"start": v(132.5, -12.7) * mm, "end": v(131.73, -12.48) * mm});
            skLineSegment(sketch, "E1092", {"start": v(131.73, -12.48) * mm, "end": v(131, -12.18) * mm});
            skLineSegment(sketch, "E1093", {"start": v(131, -12.18) * mm, "end": v(130.44, -11.7) * mm});
            skLineSegment(sketch, "E1094", {"start": v(130.44, -11.7) * mm, "end": v(130, -11.1) * mm});
            skLineSegment(sketch, "E1095", {"start": v(130, -11.1) * mm, "end": v(129.52, -10.54) * mm});
            skLineSegment(sketch, "E1096", {"start": v(129.52, -10.54) * mm, "end": v(128.96, -10.06) * mm});
            skLineSegment(sketch, "E1097", {"start": v(128.96, -10.06) * mm, "end": v(128.65, -9.86) * mm});
            skLineSegment(sketch, "E1098", {"start": v(128.65, -9.86) * mm, "end": v(128.32, -9.67) * mm});
            skLineSegment(sketch, "E1099", {"start": v(128.32, -9.67) * mm, "end": v(127.96, -9.52) * mm});
            skLineSegment(sketch, "E1100", {"start": v(127.96, -9.52) * mm, "end": v(127.76, -9.46) * mm});
            skLineSegment(sketch, "E1101", {"start": v(127.76, -9.46) * mm, "end": v(127.55, -9.42) * mm});
            skLineSegment(sketch, "E1102", {"start": v(127.55, -9.42) * mm, "end": v(127.32, -9.4) * mm});
            skLineSegment(sketch, "E1103", {"start": v(127.32, -9.4) * mm, "end": v(127.06, -9.39) * mm});
            skLineSegment(sketch, "E1104", {"start": v(127.06, -9.39) * mm, "end": v(126.75, -9.44) * mm});
            skLineSegment(sketch, "E1105", {"start": v(126.75, -9.44) * mm, "end": v(126.12, -9.75) * mm});
            skLineSegment(sketch, "E1106", {"start": v(126.12, -9.75) * mm, "end": v(124.17, -11.1) * mm});
            skLineSegment(sketch, "E1107", {"start": v(124.17, -11.1) * mm, "end": v(122, -12.08) * mm});
            skLineSegment(sketch, "E1108", {"start": v(122, -12.08) * mm, "end": v(121.41, -12.46) * mm});
            skLineSegment(sketch, "E1109", {"start": v(121.41, -12.46) * mm, "end": v(121.21, -12.7) * mm});
            skLineSegment(sketch, "E1110", {"start": v(121.21, -12.7) * mm, "end": v(121.08, -12.92) * mm});
            skLineSegment(sketch, "E1111", {"start": v(121.08, -12.92) * mm, "end": v(120.99, -13.13) * mm});
            skLineSegment(sketch, "E1112", {"start": v(120.99, -13.13) * mm, "end": v(120.92, -13.34) * mm});
            skLineSegment(sketch, "E1113", {"start": v(120.92, -13.34) * mm, "end": v(120.87, -13.54) * mm});
            skLineSegment(sketch, "E1114", {"start": v(120.87, -13.54) * mm, "end": v(120.8, -13.93) * mm});
            skLineSegment(sketch, "E1115", {"start": v(120.8, -13.93) * mm, "end": v(120.8, -14.3) * mm});
            skLineSegment(sketch, "E1116", {"start": v(120.8, -14.3) * mm, "end": v(120.81, -14.68) * mm});
            skLineSegment(sketch, "E1117", {"start": v(120.81, -14.68) * mm, "end": v(120.94, -15.4) * mm});
            skLineSegment(sketch, "E1118", {"start": v(120.94, -15.4) * mm, "end": v(121.16, -16.1) * mm});
            skLineSegment(sketch, "E1119", {"start": v(121.16, -16.1) * mm, "end": v(121.47, -16.8) * mm});
            skLineSegment(sketch, "E1120", {"start": v(121.47, -16.8) * mm, "end": v(121.58, -17.52) * mm});
            skLineSegment(sketch, "E1121", {"start": v(121.58, -17.52) * mm, "end": v(121.46, -18.3) * mm});
            skLineSegment(sketch, "E1122", {"start": v(121.46, -18.3) * mm, "end": v(121.26, -19.08) * mm});
            skLineSegment(sketch, "E1123", {"start": v(121.26, -19.08) * mm, "end": v(120.96, -19.87) * mm});
            skLineSegment(sketch, "E1124", {"start": v(120.96, -19.87) * mm, "end": v(120.6, -20.66) * mm});
            skLineSegment(sketch, "E1125", {"start": v(120.6, -20.66) * mm, "end": v(120.15, -21.46) * mm});
            skLineSegment(sketch, "E1126", {"start": v(120.15, -21.46) * mm, "end": v(119.64, -22.24) * mm});
            skLineSegment(sketch, "E1127", {"start": v(119.64, -22.24) * mm, "end": v(119.06, -23.01) * mm});
            skLineSegment(sketch, "E1128", {"start": v(119.06, -23.01) * mm, "end": v(118.4, -23.77) * mm});
            skLineSegment(sketch, "E1129", {"start": v(118.4, -23.77) * mm, "end": v(115.2, -23.63) * mm});
            skLineSegment(sketch, "E1130", {"start": v(115.2, -23.63) * mm, "end": v(112.05, -23.05) * mm});
            skLineSegment(sketch, "E1131", {"start": v(112.05, -23.05) * mm, "end": v(111.58, -22.16) * mm});
            skLineSegment(sketch, "E1132", {"start": v(111.58, -22.16) * mm, "end": v(111.18, -21.28) * mm});
            skLineSegment(sketch, "E1133", {"start": v(111.18, -21.28) * mm, "end": v(110.86, -20.4) * mm});
            skLineSegment(sketch, "E1134", {"start": v(110.86, -20.4) * mm, "end": v(110.6, -19.53) * mm});
            skLineSegment(sketch, "E1135", {"start": v(110.6, -19.53) * mm, "end": v(110.43, -18.67) * mm});
            skLineSegment(sketch, "E1136", {"start": v(110.43, -18.67) * mm, "end": v(110.32, -17.83) * mm});
            skLineSegment(sketch, "E1137", {"start": v(110.32, -17.83) * mm, "end": v(110.3, -17.02) * mm});
            skLineSegment(sketch, "E1138", {"start": v(110.3, -17.02) * mm, "end": v(110.36, -16.24) * mm});
            skLineSegment(sketch, "E1139", {"start": v(110.36, -16.24) * mm, "end": v(110.63, -15.56) * mm});
            skLineSegment(sketch, "E1140", {"start": v(110.63, -15.56) * mm, "end": v(111.08, -14.96) * mm});
            skLineSegment(sketch, "E1141", {"start": v(111.08, -14.96) * mm, "end": v(111.45, -14.32) * mm});
            skLineSegment(sketch, "E1142", {"start": v(111.45, -14.32) * mm, "end": v(111.74, -13.64) * mm});
            skLineSegment(sketch, "E1143", {"start": v(111.74, -13.64) * mm, "end": v(111.84, -13.29) * mm});
            skLineSegment(sketch, "E1144", {"start": v(111.84, -13.29) * mm, "end": v(111.9, -12.92) * mm});
            skLineSegment(sketch, "E1145", {"start": v(111.9, -12.92) * mm, "end": v(111.94, -12.52) * mm});
            skLineSegment(sketch, "E1146", {"start": v(111.94, -12.52) * mm, "end": v(111.93, -12.32) * mm});
            skLineSegment(sketch, "E1147", {"start": v(111.93, -12.32) * mm, "end": v(111.91, -12.1) * mm});
            skLineSegment(sketch, "E1148", {"start": v(111.91, -12.1) * mm, "end": v(111.87, -11.88) * mm});
            skLineSegment(sketch, "E1149", {"start": v(111.87, -11.88) * mm, "end": v(111.79, -11.63) * mm});
            skLineSegment(sketch, "E1150", {"start": v(111.79, -11.63) * mm, "end": v(111.65, -11.35) * mm});
            skLineSegment(sketch, "E1151", {"start": v(111.65, -11.35) * mm, "end": v(111.16, -10.85) * mm});
            skLineSegment(sketch, "E1152", {"start": v(111.16, -10.85) * mm, "end": v(109.26, -9.41) * mm});
            skLineSegment(sketch, "E1153", {"start": v(109.26, -9.41) * mm, "end": v(107.67, -7.65) * mm});
            skLineSegment(sketch, "E1154", {"start": v(121.06, 0) * mm, "end": v(120.95, 0.82) * mm});
            skLineSegment(sketch, "E1155", {"start": v(120.95, 0.82) * mm, "end": v(120.63, 1.59) * mm});
            skLineSegment(sketch, "E1156", {"start": v(120.63, 1.59) * mm, "end": v(120.13, 2.24) * mm});
            skLineSegment(sketch, "E1157", {"start": v(120.13, 2.24) * mm, "end": v(119.47, 2.75) * mm});
            skLineSegment(sketch, "E1158", {"start": v(119.47, 2.75) * mm, "end": v(118.7, 3.07) * mm});
            skLineSegment(sketch, "E1159", {"start": v(118.7, 3.07) * mm, "end": v(117.88, 3.17) * mm});
            skLineSegment(sketch, "E1160", {"start": v(117.88, 3.17) * mm, "end": v(117.06, 3.07) * mm});
            skLineSegment(sketch, "E1161", {"start": v(117.06, 3.07) * mm, "end": v(116.3, 2.75) * mm});
            skLineSegment(sketch, "E1162", {"start": v(116.3, 2.75) * mm, "end": v(115.64, 2.24) * mm});
            skLineSegment(sketch, "E1163", {"start": v(115.64, 2.24) * mm, "end": v(115.13, 1.59) * mm});
            skLineSegment(sketch, "E1164", {"start": v(115.13, 1.59) * mm, "end": v(114.82, 0.82) * mm});
            skLineSegment(sketch, "E1165", {"start": v(114.82, 0.82) * mm, "end": v(114.7, 0) * mm});
            skLineSegment(sketch, "E1166", {"start": v(114.7, 0) * mm, "end": v(114.82, -0.82) * mm});
            skLineSegment(sketch, "E1167", {"start": v(114.82, -0.82) * mm, "end": v(115.13, -1.59) * mm});
            skLineSegment(sketch, "E1168", {"start": v(115.13, -1.59) * mm, "end": v(115.64, -2.24) * mm});
            skLineSegment(sketch, "E1169", {"start": v(115.64, -2.24) * mm, "end": v(116.3, -2.75) * mm});
            skLineSegment(sketch, "E1170", {"start": v(116.3, -2.75) * mm, "end": v(117.06, -3.07) * mm});
            skLineSegment(sketch, "E1171", {"start": v(117.06, -3.07) * mm, "end": v(117.88, -3.18) * mm});
            skLineSegment(sketch, "E1172", {"start": v(117.88, -3.18) * mm, "end": v(118.7, -3.07) * mm});
            skLineSegment(sketch, "E1173", {"start": v(118.7, -3.07) * mm, "end": v(119.47, -2.75) * mm});
            skLineSegment(sketch, "E1174", {"start": v(119.47, -2.75) * mm, "end": v(120.13, -2.24) * mm});
            skLineSegment(sketch, "E1175", {"start": v(120.13, -2.24) * mm, "end": v(120.63, -1.59) * mm});
            skLineSegment(sketch, "E1176", {"start": v(120.63, -1.59) * mm, "end": v(120.95, -0.82) * mm});
            skLineSegment(sketch, "E1177", {"start": v(120.95, -0.82) * mm, "end": v(121.06, 0) * mm});
            skSolve(sketch);
        }
        {
            var Q0;
            Q0=makeQuery(id+"F0.imprint","IMPRINT",FACE,{"disambiguationData":[TD([[makeQuery(id+"F0.imprint","IMPRINT",EDGE,{"derivedFrom":sQuery(id+"F0.wireOp",EDGE,"E0")}),-1.0]])]});
            var Q1;
            Q1=makeQuery(id+"F0.imprint","IMPRINT",FACE,{"disambiguationData":[TD([[makeQuery(id+"F0.imprint","IMPRINT",EDGE,{"derivedFrom":sQuery(id+"F0.wireOp",EDGE,"E924")}),-1.0]])]});
            extrude(context, id + "F1", {"entities" : qUnion([Q0, Q1]), "depth" : 19.05 * mm});
        }
    });
